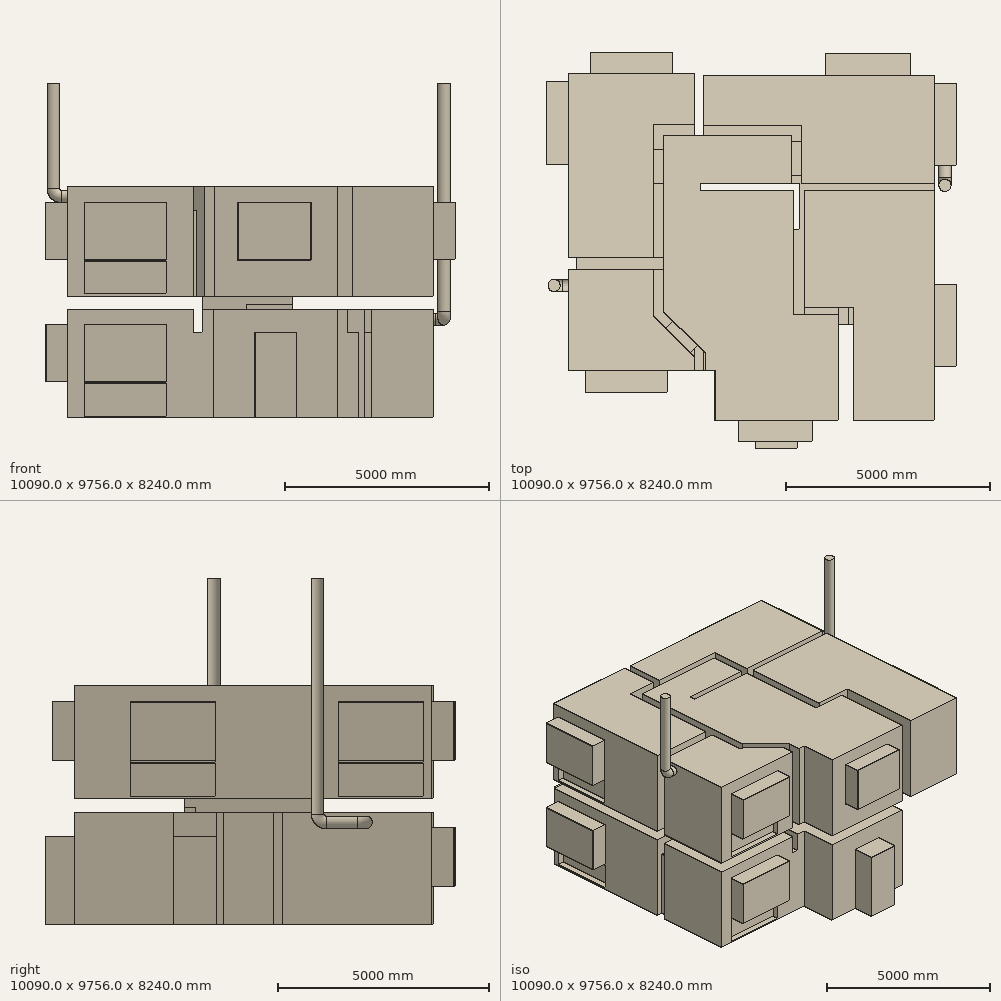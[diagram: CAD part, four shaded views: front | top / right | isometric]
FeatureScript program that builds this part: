
annotation { "Feature Type Name" : "Feature", "Feature Type Description" : "" }
export const myFeature = defineFeature(function(context is Context, id is Id, definition is map)
    precondition{}
    {
        {
            var Q0;
            Q0=qCreatedBy(makeId("Top.planeOp"),FACE);
            var sketch = newSketch(context, id + "F0", { "sketchPlane" : qUnion([Q0])});
            skLineSegment(sketch, "E0.bottom", {"start": v(-1549.14, 3434.73) * mm, "end": v(1546.86, 3434.73) * mm});
            skLineSegment(sketch, "E0.top", {"start": v(-1549.14, -1072.27) * mm, "end": v(1546.86, -1072.27) * mm});
            skLineSegment(sketch, "E0.left", {"start": v(-1549.14, 3434.73) * mm, "end": v(-1549.14, -1072.27) * mm});
            skLineSegment(sketch, "E0.right", {"start": v(1546.86, 3434.73) * mm, "end": v(1546.86, -1072.27) * mm});
            skSolve(sketch);
        }
        {
            var Q0;
            Q0=makeQuery(id+"F0.imprint","IMPRINT",FACE,{"disambiguationData":[TD([[makeQuery(id+"F0.imprint","IMPRINT",EDGE,{"derivedFrom":sQuery(id+"F0.wireOp",EDGE,"E0.bottom")}),-1.0]])]});
            extrude(context, id + "F1", {"entities" : qUnion([Q0]), "depth" : 2680 * mm});
        }
        {
            var Q0;
            Q0=makeQuery(id+"F1.opExtrude","SWEPT_FACE",FACE,{"disambiguationData":[OSD([sQuery(id+"F0.wireOp",EDGE,"E0.bottom")])]});
            var sketch = newSketch(context, id + "F2", { "sketchPlane" : qUnion([Q0])});
            skLineSegment(sketch, "E1.bottom", {"start": v(-1013.86, 2300) * mm, "end": v(1011.14, 2300) * mm});
            skLineSegment(sketch, "E1.top", {"start": v(-1013.86, 900) * mm, "end": v(1011.14, 900) * mm});
            skLineSegment(sketch, "E1.left", {"start": v(-1013.86, 2300) * mm, "end": v(-1013.86, 900) * mm});
            skLineSegment(sketch, "E1.right", {"start": v(1011.14, 2300) * mm, "end": v(1011.14, 900) * mm});
            skSolve(sketch);
        }
        {
            var Q0;
            Q0=qSketchRegion(id+"F2",true);
            extrude(context, id + "F3", {"entities" : qUnion([Q0]), "operationType" : NewBodyOperationType.ADD, "depth" : 532 * mm});
        }
        {
            var Q0;
            Q0=makeQuery(id+"F1.opExtrude","SWEPT_FACE",FACE,{"disambiguationData":[OSD([sQuery(id+"F0.wireOp",EDGE,"E0.left")])]});
            var sketch = newSketch(context, id + "F4", { "sketchPlane" : qUnion([Q0])});
            skLineSegment(sketch, "E2.bottom", {"start": v(-3238.73, 2300) * mm, "end": v(-1213.73, 2300) * mm});
            skLineSegment(sketch, "E2.top", {"start": v(-3238.73, 900) * mm, "end": v(-1213.73, 900) * mm});
            skLineSegment(sketch, "E2.left", {"start": v(-3238.73, 2300) * mm, "end": v(-3238.73, 900) * mm});
            skLineSegment(sketch, "E2.right", {"start": v(-1213.73, 2300) * mm, "end": v(-1213.73, 900) * mm});
            skSolve(sketch);
        }
        {
            var Q0;
            Q0=makeQuery(id+"F4.imprint","IMPRINT",FACE,{"disambiguationData":[TD([[makeQuery(id+"F4.imprint","IMPRINT",EDGE,{"derivedFrom":sQuery(id+"F4.wireOp",EDGE,"E2.bottom")}),-1.0]])]});
            extrude(context, id + "F5", {"entities" : qUnion([Q0]), "operationType" : NewBodyOperationType.ADD, "depth" : 532 * mm});
        }
        {
            var Q0;
            Q0=makeQuery(id+"F1.opExtrude","SWEPT_FACE",FACE,{"disambiguationData":[OSD([sQuery(id+"F0.wireOp",EDGE,"E0.bottom")])]});
            var sketch = newSketch(context, id + "F6", { "sketchPlane" : qUnion([Q0])});
            skLineSegment(sketch, "E3", {"start": v(1011.14, 900) * mm, "end": v(-1013.86, 900) * mm});
            skLineSegment(sketch, "E4.left", {"start": v(-1013.86, 835) * mm, "end": v(-1013.86, 35) * mm});
            skLineSegment(sketch, "E5.bottom", {"start": v(-1013.86, 835) * mm, "end": v(1011.14, 835) * mm});
            skLineSegment(sketch, "E5.top", {"start": v(-1013.86, 35) * mm, "end": v(1011.14, 35) * mm});
            skLineSegment(sketch, "E5.right", {"start": v(1011.14, 835) * mm, "end": v(1011.14, 35) * mm});
            skSolve(sketch);
        }
        {
            var Q0;
            Q0=makeQuery(id+"F6.imprint","IMPRINT",FACE,{"disambiguationData":[TD([[makeQuery(id+"F6.imprint","IMPRINT",EDGE,{"derivedFrom":sQuery(id+"F6.wireOp",EDGE,"E5.bottom")}),-1.0]])]});
            extrude(context, id + "F7", {"entities" : qUnion([Q0]), "operationType" : NewBodyOperationType.REMOVE, "oppositeDirection" : true, "depth" : 200 * mm});
        }
        {
            var Q0;
            Q0=makeQuery(id+"F1.opExtrude","CAP_FACE",FACE,{"disambiguationData":[OSD([sQuery(id+"F0.wireOp",EDGE,"E0.bottom"),sQuery(id+"F0.wireOp",EDGE,"E0.top"),sQuery(id+"F0.wireOp",EDGE,"E0.left"),sQuery(id+"F0.wireOp",EDGE,"E0.right")])],"isStart":true});
            var sketch = newSketch(context, id + "F8", { "sketchPlane" : qUnion([Q0])});
            skLineSegment(sketch, "E6", {"start": v(-1351.14, 1072.27) * mm, "end": v(-1351.14, 1375.27) * mm});
            skLineSegment(sketch, "E7", {"start": v(-1351.14, 1375.27) * mm, "end": v(1348.86, 1375.27) * mm});
            skLineSegment(sketch, "E8", {"start": v(1348.86, 1375.27) * mm, "end": v(1348.86, 1072.27) * mm});
            skLineSegment(sketch, "E9", {"start": v(1348.86, 1072.27) * mm, "end": v(-1351.14, 1072.27) * mm});
            skSolve(sketch);
        }
        {
            var Q0;
            Q0=makeQuery(id+"F8.imprint","IMPRINT",FACE,{"disambiguationData":[TD([[makeQuery(id+"F8.imprint","IMPRINT",EDGE,{"derivedFrom":sQuery(id+"F8.wireOp",EDGE,"E6")}),-1.0]])]});
            extrude(context, id + "F9", {"entities" : qUnion([Q0]), "operationType" : NewBodyOperationType.ADD, "oppositeDirection" : true, "depth" : 2100 * mm});
        }
        {
            var Q0;
            Q0=makeQuery(id+"F9.boolean.opBoolean","MERGE",FACE,{"derivedFrom":[makeQuery(id+"F1.opExtrude","CAP_FACE",FACE,{"disambiguationData":[OSD([sQuery(id+"F0.wireOp",EDGE,"E0.bottom"),sQuery(id+"F0.wireOp",EDGE,"E0.top"),sQuery(id+"F0.wireOp",EDGE,"E0.left"),sQuery(id+"F0.wireOp",EDGE,"E0.right")])],"isStart":true}),makeQuery(id+"F9.opExtrude","CAP_FACE",FACE,{"disambiguationData":[OSD([sQuery(id+"F8.wireOp",EDGE,"E6"),sQuery(id+"F8.wireOp",EDGE,"E7"),sQuery(id+"F8.wireOp",EDGE,"E8"),sQuery(id+"F8.wireOp",EDGE,"E9")])],"isStart":true})]});
            var sketch = newSketch(context, id + "F10", { "sketchPlane" : qUnion([Q0])});
            skLineSegment(sketch, "E10.bottom", {"start": v(-1549.14, 1375.27) * mm, "end": v(1546.86, 1375.27) * mm});
            skLineSegment(sketch, "E10.top", {"start": v(-1549.14, 3872.27) * mm, "end": v(1546.86, 3872.27) * mm});
            skLineSegment(sketch, "E10.left", {"start": v(-1549.14, 1375.27) * mm, "end": v(-1549.14, 3872.27) * mm});
            skLineSegment(sketch, "E10.right", {"start": v(1546.86, 1375.27) * mm, "end": v(1546.86, 3872.27) * mm});
            skLineSegment(sketch, "E11", {"start": v(-1549.14, 1375.27) * mm, "end": v(-1351.14, 1375.27) * mm});
            skSolve(sketch);
        }
        {
            var Q0;
            Q0=qSketchRegion(id+"F10",true);
            extrude(context, id + "F11", {"entities" : qUnion([Q0]), "operationType" : NewBodyOperationType.ADD, "oppositeDirection" : true, "depth" : 2680 * mm});
        }
        {
            var Q0;
            Q0=makeQuery(id+"F11.boolean.opBoolean","MERGE",FACE,{"derivedFrom":[makeQuery(id+"F9.boolean.opBoolean","MERGE",FACE,{"derivedFrom":[makeQuery(id+"F1.opExtrude","CAP_FACE",FACE,{"disambiguationData":[OSD([sQuery(id+"F0.wireOp",EDGE,"E0.bottom"),sQuery(id+"F0.wireOp",EDGE,"E0.top"),sQuery(id+"F0.wireOp",EDGE,"E0.left"),sQuery(id+"F0.wireOp",EDGE,"E0.right")])],"isStart":true}),makeQuery(id+"F9.opExtrude","CAP_FACE",FACE,{"disambiguationData":[OSD([sQuery(id+"F8.wireOp",EDGE,"E6"),sQuery(id+"F8.wireOp",EDGE,"E7"),sQuery(id+"F8.wireOp",EDGE,"E8"),sQuery(id+"F8.wireOp",EDGE,"E9")])],"isStart":true})]}),makeQuery(id+"F11.opExtrude","CAP_FACE",FACE,{"disambiguationData":[OSD([sQuery(id+"F10.wireOp",EDGE,"E10.bottom"),sQuery(id+"F10.wireOp",EDGE,"E10.top"),sQuery(id+"F10.wireOp",EDGE,"E10.left"),sQuery(id+"F10.wireOp",EDGE,"E10.right"),sQuery(id+"F10.wireOp",EDGE,"E11")])],"isStart":true})]});
            var sketch = newSketch(context, id + "F12", { "sketchPlane" : qUnion([Q0])});
            skLineSegment(sketch, "E12.bottom", {"start": v(1546.86, 3872.27) * mm, "end": v(1765.86, 3872.27) * mm});
            skLineSegment(sketch, "E12.top", {"start": v(1546.86, 2526.27) * mm, "end": v(1765.86, 2526.27) * mm});
            skLineSegment(sketch, "E12.left", {"start": v(1546.86, 3872.27) * mm, "end": v(1546.86, 2526.27) * mm});
            skLineSegment(sketch, "E12.right", {"start": v(1765.86, 3872.27) * mm, "end": v(1765.86, 2526.27) * mm});
            skSolve(sketch);
        }
        {
            var Q0;
            Q0=makeQuery(id+"F12.imprint","IMPRINT",FACE,{"disambiguationData":[TD([[makeQuery(id+"F12.imprint","IMPRINT",EDGE,{"derivedFrom":sQuery(id+"F12.wireOp",EDGE,"E12.bottom")}),-1.0]])]});
            extrude(context, id + "F13", {"entities" : qUnion([Q0]), "operationType" : NewBodyOperationType.ADD, "oppositeDirection" : true, "depth" : 2100 * mm});
        }
        {
            var Q0;
            Q0=makeQuery(id+"F13.boolean.opBoolean","MERGE",FACE,{"derivedFrom":[makeQuery(id+"F11.opExtrude","SWEPT_FACE",FACE,{"disambiguationData":[OSD([sQuery(id+"F10.wireOp",EDGE,"E10.top")])]}),makeQuery(id+"F13.opExtrude","SWEPT_FACE",FACE,{"disambiguationData":[OSD([sQuery(id+"F12.wireOp",EDGE,"E12.bottom")])]})]});
            var sketch = newSketch(context, id + "F14", { "sketchPlane" : qUnion([Q0])});
            skLineSegment(sketch, "E13.bottom", {"start": v(-1134.15, 2296.53) * mm, "end": v(890.85, 2296.53) * mm});
            skLineSegment(sketch, "E13.top", {"start": v(-1134.15, 896.53) * mm, "end": v(890.85, 896.53) * mm});
            skLineSegment(sketch, "E13.left", {"start": v(-1134.15, 2296.53) * mm, "end": v(-1134.15, 896.53) * mm});
            skLineSegment(sketch, "E13.right", {"start": v(890.85, 2296.53) * mm, "end": v(890.85, 896.53) * mm});
            skSolve(sketch);
        }
        {
            var Q0;
            Q0=makeQuery(id+"F14.imprint","IMPRINT",FACE,{"disambiguationData":[TD([[makeQuery(id+"F14.imprint","IMPRINT",EDGE,{"derivedFrom":sQuery(id+"F14.wireOp",EDGE,"E13.bottom")}),-1.0]])]});
            extrude(context, id + "F15", {"entities" : qUnion([Q0]), "operationType" : NewBodyOperationType.ADD, "depth" : 532 * mm});
        }
        {
            var Q0;
            Q0=makeQuery(id+"F12.imprint","IMPRINT",FACE,{"disambiguationData":[TD([[makeQuery(id+"F12.imprint","IMPRINT",EDGE,{"derivedFrom":sQuery(id+"F12.wireOp",EDGE,"E12.bottom")}),-1.0]])]});
            var sketch = newSketch(context, id + "F16", { "sketchPlane" : qUnion([Q0])});
            skLineSegment(sketch, "E14", {"start": v(1765.86, 3872.27) * mm, "end": v(2057.86, 3872.27) * mm});
            skLineSegment(sketch, "E15", {"start": v(2057.86, 3872.27) * mm, "end": v(2057.86, 5091.27) * mm});
            skLineSegment(sketch, "E16", {"start": v(1765.86, 3872.27) * mm, "end": v(1765.86, 2474.27) * mm});
            skLineSegment(sketch, "E17", {"start": v(1765.86, 2474.27) * mm, "end": v(2915.86, 2474.27) * mm});
            skLineSegment(sketch, "E18", {"start": v(2915.86, 2474.27) * mm, "end": v(2915.86, 2739.27) * mm});
            skLineSegment(sketch, "E19", {"start": v(2915.86, 2739.27) * mm, "end": v(5096.86, 2739.27) * mm});
            skLineSegment(sketch, "E20", {"start": v(5096.86, 2739.27) * mm, "end": v(5096.86, 5091.27) * mm});
            skLineSegment(sketch, "E21", {"start": v(2057.86, 5091.27) * mm, "end": v(5096.86, 5091.27) * mm});
            skSolve(sketch);
        }
        {
            var Q0;
            {var subQ1=sQuery(id+"F16.wireOp",EDGE,"E14");Q0=makeQuery(id+"F16.imprint","IMPRINT",FACE,{"disambiguationData":[TD([[makeQuery(id+"F16.imprint","IMPRINT",EDGE,{"derivedFrom":subQ1}),-1.0]])]});}
            extrude(context, id + "F17", {"entities" : qUnion([Q0]), "operationType" : NewBodyOperationType.ADD, "oppositeDirection" : true, "depth" : 2680 * mm});
        }
        {
            var Q0;
            Q0=makeQuery(id+"F17.boolean.opBoolean","MERGE",FACE,{"derivedFrom":[makeQuery(id+"F13.boolean.opBoolean","MERGE",FACE,{"derivedFrom":[makeQuery(id+"F11.boolean.opBoolean","MERGE",FACE,{"derivedFrom":[makeQuery(id+"F9.boolean.opBoolean","MERGE",FACE,{"derivedFrom":[makeQuery(id+"F1.opExtrude","CAP_FACE",FACE,{"disambiguationData":[OSD([sQuery(id+"F0.wireOp",EDGE,"E0.bottom"),sQuery(id+"F0.wireOp",EDGE,"E0.top"),sQuery(id+"F0.wireOp",EDGE,"E0.left"),sQuery(id+"F0.wireOp",EDGE,"E0.right")])],"isStart":true}),makeQuery(id+"F9.opExtrude","CAP_FACE",FACE,{"disambiguationData":[OSD([sQuery(id+"F8.wireOp",EDGE,"E6"),sQuery(id+"F8.wireOp",EDGE,"E7"),sQuery(id+"F8.wireOp",EDGE,"E8"),sQuery(id+"F8.wireOp",EDGE,"E9")])],"isStart":true})]}),makeQuery(id+"F11.opExtrude","CAP_FACE",FACE,{"disambiguationData":[OSD([sQuery(id+"F10.wireOp",EDGE,"E10.bottom"),sQuery(id+"F10.wireOp",EDGE,"E10.top"),sQuery(id+"F10.wireOp",EDGE,"E10.left"),sQuery(id+"F10.wireOp",EDGE,"E10.right"),sQuery(id+"F10.wireOp",EDGE,"E11")])],"isStart":true})]}),makeQuery(id+"F13.opExtrude","CAP_FACE",FACE,{"disambiguationData":[OSD([sQuery(id+"F12.wireOp",EDGE,"E12.bottom"),sQuery(id+"F12.wireOp",EDGE,"E12.top"),sQuery(id+"F12.wireOp",EDGE,"E12.left"),sQuery(id+"F12.wireOp",EDGE,"E12.right")])],"isStart":true})]}),makeQuery(id+"F17.opExtrude","CAP_FACE",FACE,{"disambiguationData":[OSD([sQuery(id+"F16.wireOp",EDGE,"E14"),sQuery(id+"F16.wireOp",EDGE,"E15"),sQuery(id+"F16.wireOp",EDGE,"E16"),sQuery(id+"F16.wireOp",EDGE,"E17"),sQuery(id+"F16.wireOp",EDGE,"E18"),sQuery(id+"F16.wireOp",EDGE,"E19"),sQuery(id+"F16.wireOp",EDGE,"E20"),sQuery(id+"F16.wireOp",EDGE,"E21")])],"isStart":true})]});
            var sketch = newSketch(context, id + "F18", { "sketchPlane" : qUnion([Q0])});
            skLineSegment(sketch, "E22.bottom", {"start": v(3064.86, 5091.27) * mm, "end": v(4089.86, 5091.27) * mm});
            skLineSegment(sketch, "E22.top", {"start": v(3064.86, 5789.27) * mm, "end": v(4089.86, 5789.27) * mm});
            skLineSegment(sketch, "E22.left", {"start": v(3064.86, 5091.27) * mm, "end": v(3064.86, 5789.27) * mm});
            skLineSegment(sketch, "E22.right", {"start": v(4089.86, 5091.27) * mm, "end": v(4089.86, 5789.27) * mm});
            skSolve(sketch);
        }
        {
            var Q0;
            Q0=makeQuery(id+"F18.imprint","IMPRINT",FACE,{"disambiguationData":[TD([[makeQuery(id+"F18.imprint","IMPRINT",EDGE,{"derivedFrom":sQuery(id+"F18.wireOp",EDGE,"E22.bottom")}),1.0]])]});
            extrude(context, id + "F19", {"entities" : qUnion([Q0]), "operationType" : NewBodyOperationType.ADD, "oppositeDirection" : true, "depth" : 2100 * mm});
        }
        {
            var Q0;
            {var subQ0=sQuery(id+"F16.wireOp",EDGE,"E14");Q0=makeQuery(id+"F16.imprint","IMPRINT",FACE,{"disambiguationData":[TD([[makeQuery(id+"F16.imprint","IMPRINT",EDGE,{"derivedFrom":subQ0}),-1.0]])]});}
            var sketch = newSketch(context, id + "F20", { "sketchPlane" : qUnion([Q0])});
            skLineSegment(sketch, "E23.bottom", {"start": v(1765.86, 2474.27) * mm, "end": v(3985.86, 2474.27) * mm});
            skLineSegment(sketch, "E23.top", {"start": v(1765.86, -565.73) * mm, "end": v(3985.86, -565.73) * mm});
            skLineSegment(sketch, "E23.left", {"start": v(1765.86, 2474.27) * mm, "end": v(1765.86, -565.73) * mm});
            skLineSegment(sketch, "E23.right", {"start": v(3985.86, 2474.27) * mm, "end": v(3985.86, -565.73) * mm});
            skSolve(sketch);
        }
        {
            var Q0;
            Q0=makeQuery(id+"F20.imprint","IMPRINT",FACE,{"disambiguationData":[TD([[makeQuery(id+"F20.imprint","IMPRINT",EDGE,{"derivedFrom":sQuery(id+"F20.wireOp",EDGE,"E23.top")}),1.0]])]});
            extrude(context, id + "F21", {"entities" : qUnion([Q0]), "oppositeDirection" : true, "depth" : 3000 * mm});
        }
        {
            var Q0;
            Q0=makeQuery(id+"F21.opExtrude","SWEPT_FACE",FACE,{"disambiguationData":[OSD([sQuery(id+"F20.wireOp",EDGE,"E23.left")])]});
            var sketch = newSketch(context, id + "F22", { "sketchPlane" : qUnion([Q0])});
            skLineSegment(sketch, "E24.MirrorCS", {"start": v(1199.27, 1020) * mm, "end": v(944.27, 1020) * mm});
            skLineSegment(sketch, "E25.MirrorCS", {"start": v(1709.27, 680) * mm, "end": v(1454.27, 680) * mm});
            skLineSegment(sketch, "E26.MirrorCS", {"start": v(2219.27, 340) * mm, "end": v(1964.27, 340) * mm});
            skLineSegment(sketch, "E27.MirrorCS", {"start": v(2474.27, 0) * mm, "end": v(2219.27, 0) * mm});
            skLineSegment(sketch, "E28.MirrorCS", {"start": v(1964.27, 340) * mm, "end": v(1964.27, 510) * mm});
            skLineSegment(sketch, "E29.MirrorCS", {"start": v(1454.27, 680) * mm, "end": v(1454.27, 850) * mm});
            skLineSegment(sketch, "E30.MirrorCS", {"start": v(1709.27, 510) * mm, "end": v(1709.27, 680) * mm});
            skLineSegment(sketch, "E31.MirrorCS", {"start": v(1199.27, 850) * mm, "end": v(1199.27, 1020) * mm});
            skLineSegment(sketch, "E32.MirrorCS", {"start": v(1454.27, 850) * mm, "end": v(1199.27, 850) * mm});
            skLineSegment(sketch, "E33.MirrorCS", {"start": v(-565.73, 1530) * mm, "end": v(-565.73, 1330) * mm});
            skLineSegment(sketch, "E34.MirrorCS", {"start": v(2219.27, 170) * mm, "end": v(2219.27, 340) * mm});
            skLineSegment(sketch, "E35.MirrorCS", {"start": v(2474.27, 170) * mm, "end": v(2219.27, 170) * mm});
            skLineSegment(sketch, "E36.MirrorCS", {"start": v(1964.27, 510) * mm, "end": v(1709.27, 510) * mm});
            skLineSegment(sketch, "E37.MirrorCS", {"start": v(2474.27, 0) * mm, "end": v(2474.27, 170) * mm});
            skLineSegment(sketch, "E38.MirrorCS", {"start": v(2474.27, 170) * mm, "end": v(2474.27, 0) * mm});
            skLineSegment(sketch, "E39", {"start": v(2219.27, 0) * mm, "end": v(179.27, 1330) * mm});
            skLineSegment(sketch, "E40", {"start": v(944.27, 1020) * mm, "end": v(944.27, 1190) * mm});
            skLineSegment(sketch, "E41", {"start": v(944.27, 1190) * mm, "end": v(689.27, 1190) * mm});
            skLineSegment(sketch, "E42", {"start": v(689.27, 1190) * mm, "end": v(689.27, 1330) * mm});
            skLineSegment(sketch, "E43", {"start": v(689.27, 1330) * mm, "end": v(434.27, 1330) * mm});
            skLineSegment(sketch, "E44", {"start": v(434.27, 1330) * mm, "end": v(434.27, 1530) * mm});
            skLineSegment(sketch, "E45", {"start": v(434.27, 1530) * mm, "end": v(-565.73, 1530) * mm});
            skLineSegment(sketch, "E46", {"start": v(-565.73, 1330) * mm, "end": v(179.27, 1330) * mm});
            skSolve(sketch);
        }
        {
            var Q0;
            Q0=qSketchRegion(id+"F22",true);
            extrude(context, id + "F23", {"entities" : qUnion([Q0]), "operationType" : NewBodyOperationType.REMOVE, "oppositeDirection" : true, "depth" : 1110 * mm});
        }
        {
            var Q0;
            Q0=makeQuery(id+"F21.opExtrude","SWEPT_FACE",FACE,{"disambiguationData":[OSD([sQuery(id+"F20.wireOp",EDGE,"E23.right")])]});
            var sketch = newSketch(context, id + "F24", { "sketchPlane" : qUnion([Q0])});
            skLineSegment(sketch, "E47", {"start": v(565.73, 1530) * mm, "end": v(-689.27, 1530) * mm});
            skLineSegment(sketch, "E48", {"start": v(-689.27, 1530) * mm, "end": v(-689.27, 1710) * mm});
            skLineSegment(sketch, "E49", {"start": v(-689.27, 1710) * mm, "end": v(-944.27, 1710) * mm});
            skLineSegment(sketch, "E50", {"start": v(-944.27, 1710) * mm, "end": v(-944.27, 1890) * mm});
            skLineSegment(sketch, "E51", {"start": v(-944.27, 1890) * mm, "end": v(-1199.27, 1890) * mm});
            skLineSegment(sketch, "E52", {"start": v(-1199.27, 1890) * mm, "end": v(-1199.27, 2070) * mm});
            skLineSegment(sketch, "E53", {"start": v(-1199.27, 2070) * mm, "end": v(-1454.27, 2070) * mm});
            skLineSegment(sketch, "E54", {"start": v(-1454.27, 2070) * mm, "end": v(-1454.27, 2250) * mm});
            skLineSegment(sketch, "E55", {"start": v(-1454.27, 2250) * mm, "end": v(-1709.27, 2250) * mm});
            skLineSegment(sketch, "E56", {"start": v(-1709.27, 2430) * mm, "end": v(-1709.27, 2250) * mm});
            skLineSegment(sketch, "E57", {"start": v(565.73, 1530) * mm, "end": v(565.73, 1330) * mm});
            skLineSegment(sketch, "E58", {"start": v(-689.27, 1330) * mm, "end": v(565.73, 1330) * mm});
            skLineSegment(sketch, "E59", {"start": v(-1709.27, 2430) * mm, "end": v(-1964.27, 2430) * mm});
            skLineSegment(sketch, "E60", {"start": v(-1964.27, 2430) * mm, "end": v(-1964.27, 2610) * mm});
            skLineSegment(sketch, "E61", {"start": v(-1964.27, 2610) * mm, "end": v(-2219.27, 2610) * mm});
            skLineSegment(sketch, "E62", {"start": v(-2219.27, 2610) * mm, "end": v(-2219.27, 2790) * mm});
            skLineSegment(sketch, "E63", {"start": v(-2219.27, 2790) * mm, "end": v(-2474.27, 2790) * mm});
            skLineSegment(sketch, "E64", {"start": v(-2474.27, 2651.89) * mm, "end": v(-689.27, 1330) * mm});
            skLineSegment(sketch, "E65", {"start": v(-2474.27, 2651.89) * mm, "end": v(-2474.27, 2790) * mm});
            skLineSegment(sketch, "E66", {"start": v(565.73, 1330) * mm, "end": v(565.73, 1530) * mm});
            skLineSegment(sketch, "E67", {"start": v(-689.27, 1530) * mm, "end": v(565.73, 1530) * mm});
            skSolve(sketch);
        }
        {
            var Q0;
            Q0=makeQuery(id+"F24.imprint","IMPRINT",FACE,{"disambiguationData":[TD([[makeQuery(id+"F24.imprint","IMPRINT",EDGE,{"derivedFrom":sQuery(id+"F24.wireOp",EDGE,"E48")}),1.0]])]});
            extrude(context, id + "F25", {"entities" : qUnion([Q0]), "operationType" : NewBodyOperationType.REMOVE, "oppositeDirection" : true, "depth" : 1120 * mm});
        }
        {
            var Q0;
            Q0=makeQuery(id+"F17.opExtrude","CAP_FACE",FACE,{"disambiguationData":[OSD([sQuery(id+"F16.wireOp",EDGE,"E14"),sQuery(id+"F16.wireOp",EDGE,"E15"),sQuery(id+"F16.wireOp",EDGE,"E16"),sQuery(id+"F16.wireOp",EDGE,"E17"),sQuery(id+"F16.wireOp",EDGE,"E18"),sQuery(id+"F16.wireOp",EDGE,"E19"),sQuery(id+"F16.wireOp",EDGE,"E20"),sQuery(id+"F16.wireOp",EDGE,"E21")])],"isStart":false});
            var sketch = newSketch(context, id + "F26", { "sketchPlane" : qUnion([Q0])});
            skLineSegment(sketch, "E68", {"start": v(5096.86, -2739.27) * mm, "end": v(5356.86, -2739.27) * mm});
            skLineSegment(sketch, "E69", {"start": v(5221.86, -1714.27) * mm, "end": v(5221.86, -1554.27) * mm});
            skLineSegment(sketch, "E70", {"start": v(5221.86, -1554.27) * mm, "end": v(5771.86, -1554.27) * mm});
            skLineSegment(sketch, "E71", {"start": v(5771.86, -1554.27) * mm, "end": v(5771.86, -1454.27) * mm});
            skLineSegment(sketch, "E72", {"start": v(5771.86, -629.27) * mm, "end": v(5771.86, -354.27) * mm});
            skLineSegment(sketch, "E73", {"start": v(5771.86, -354.27) * mm, "end": v(5421.86, -354.27) * mm});
            skLineSegment(sketch, "E74", {"start": v(5421.86, -354.27) * mm, "end": v(5421.86, -142.27) * mm});
            skLineSegment(sketch, "E75", {"start": v(7471.86, 3404.73) * mm, "end": v(6893.86, 3404.73) * mm});
            skLineSegment(sketch, "E76", {"start": v(4681.86, 3404.73) * mm, "end": v(1765.86, 3404.73) * mm});
            skLineSegment(sketch, "E77", {"start": v(1765.86, 3404.73) * mm, "end": v(1765.86, 747.73) * mm});
            skLineSegment(sketch, "E78", {"start": v(1765.86, 747.73) * mm, "end": v(4146.86, 747.73) * mm});
            skLineSegment(sketch, "E79", {"start": v(4146.86, 747.73) * mm, "end": v(4146.86, -384.27) * mm});
            skLineSegment(sketch, "E80", {"start": v(5096.86, -2739.27) * mm, "end": v(2915.86, -2739.27) * mm});
            skLineSegment(sketch, "E81", {"start": v(2915.86, -2739.27) * mm, "end": v(2915.86, -2474.27) * mm});
            skLineSegment(sketch, "E82", {"start": v(2915.86, -2474.27) * mm, "end": v(3985.86, -2474.27) * mm});
            skLineSegment(sketch, "E83", {"start": v(3985.86, -2474.27) * mm, "end": v(3985.86, -384.27) * mm});
            skLineSegment(sketch, "E84", {"start": v(3985.86, -384.27) * mm, "end": v(4146.86, -384.27) * mm});
            skLineSegment(sketch, "E85", {"start": v(5771.86, -629.27) * mm, "end": v(5771.86, -1454.27) * mm});
            skLineSegment(sketch, "E86", {"start": v(4681.86, 3404.73) * mm, "end": v(6893.86, 3404.73) * mm});
            skLineSegment(sketch, "E87", {"start": v(5356.86, -2739.27) * mm, "end": v(5356.86, -1714.27) * mm});
            skLineSegment(sketch, "E88", {"start": v(5356.86, -1714.27) * mm, "end": v(5221.86, -1714.27) * mm});
            skLineSegment(sketch, "E89", {"start": v(7471.86, 3404.73) * mm, "end": v(7471.86, -142.27) * mm});
            skLineSegment(sketch, "E90", {"start": v(5421.86, -142.27) * mm, "end": v(7471.86, -142.27) * mm});
            skSolve(sketch);
        }
        {
            var Q0;
            Q0=makeQuery(id+"F26.imprint","IMPRINT",FACE,{"disambiguationData":[TD([[makeQuery(id+"F26.imprint","IMPRINT",EDGE,{"derivedFrom":sQuery(id+"F26.wireOp",EDGE,"E68")}),1.0]])]});
            extrude(context, id + "F27", {"entities" : qUnion([Q0]), "oppositeDirection" : true, "depth" : 2680 * mm});
        }
        {
            var Q0;
            Q0=makeQuery(id+"F27.opExtrude","SWEPT_FACE",FACE,{"disambiguationData":[OSD([sQuery(id+"F26.wireOp",EDGE,"E75"),sQuery(id+"F26.wireOp",EDGE,"E76"),sQuery(id+"F26.wireOp",EDGE,"E86")])]});
            var sketch = newSketch(context, id + "F28", { "sketchPlane" : qUnion([Q0])});
            skLineSegment(sketch, "E91.bottom", {"start": v(-6883.86, 2300) * mm, "end": v(-4883.86, 2300) * mm});
            skLineSegment(sketch, "E91.top", {"start": v(-6883.86, 900) * mm, "end": v(-4883.86, 900) * mm});
            skLineSegment(sketch, "E91.left", {"start": v(-6883.86, 2300) * mm, "end": v(-6883.86, 900) * mm});
            skLineSegment(sketch, "E91.right", {"start": v(-4883.86, 2300) * mm, "end": v(-4883.86, 900) * mm});
            skSolve(sketch);
        }
        {
            var Q0;
            Q0=makeQuery(id+"F28.imprint","IMPRINT",FACE,{"disambiguationData":[TD([[makeQuery(id+"F28.imprint","IMPRINT",EDGE,{"derivedFrom":sQuery(id+"F28.wireOp",EDGE,"E91.bottom")}),-1.0]])]});
            extrude(context, id + "F29", {"entities" : qUnion([Q0]), "operationType" : NewBodyOperationType.ADD, "depth" : 532 * mm});
        }
        {
            var Q0;
            Q0=makeQuery(id+"F27.opExtrude","SWEPT_FACE",FACE,{"disambiguationData":[OSD([sQuery(id+"F26.wireOp",EDGE,"E71"),sQuery(id+"F26.wireOp",EDGE,"E72"),sQuery(id+"F26.wireOp",EDGE,"E85")])]});
            var sketch = newSketch(context, id + "F30", { "sketchPlane" : qUnion([Q0])});
            skLineSegment(sketch, "E92.bottom", {"start": v(-1454.27, 2100) * mm, "end": v(-629.27, 2100) * mm});
            skLineSegment(sketch, "E92.top", {"start": v(-1454.27, 0) * mm, "end": v(-629.27, 0) * mm});
            skLineSegment(sketch, "E92.left", {"start": v(-1454.27, 2100) * mm, "end": v(-1454.27, 0) * mm});
            skLineSegment(sketch, "E92.right", {"start": v(-629.27, 2100) * mm, "end": v(-629.27, 0) * mm});
            skSolve(sketch);
        }
        {
            var Q0;
            Q0=makeQuery(id+"F30.imprint","IMPRINT",FACE,{"disambiguationData":[TD([[makeQuery(id+"F30.imprint","IMPRINT",EDGE,{"derivedFrom":sQuery(id+"F30.wireOp",EDGE,"E92.bottom")}),-1.0]])]});
            extrude(context, id + "F31", {"entities" : qUnion([Q0]), "operationType" : NewBodyOperationType.ADD, "depth" : 160 * mm});
        }
        {
            var Q0;
            Q0=makeQuery(id+"F31.opExtrude","CAP_FACE",FACE,{"disambiguationData":[OSD([sQuery(id+"F30.wireOp",EDGE,"E92.bottom"),sQuery(id+"F30.wireOp",EDGE,"E92.top"),sQuery(id+"F30.wireOp",EDGE,"E92.left"),sQuery(id+"F30.wireOp",EDGE,"E92.right")])],"isStart":false});
            var sketch = newSketch(context, id + "F32", { "sketchPlane" : qUnion([Q0])});
            skLineSegment(sketch, "E93.bottom", {"start": v(-1554.27, 2680) * mm, "end": v(-354.27, 2680) * mm});
            skLineSegment(sketch, "E93.top", {"start": v(-1554.27, 0) * mm, "end": v(-354.27, 0) * mm});
            skLineSegment(sketch, "E93.left", {"start": v(-1554.27, 2680) * mm, "end": v(-1554.27, 0) * mm});
            skLineSegment(sketch, "E93.right", {"start": v(-354.27, 2680) * mm, "end": v(-354.27, 0) * mm});
            skSolve(sketch);
        }
        {
            var Q0;
            Q0=qSketchRegion(id+"F32",true);
            extrude(context, id + "F33", {"entities" : qUnion([Q0]), "operationType" : NewBodyOperationType.ADD, "depth" : 1540 * mm});
        }
        {
            var Q0;
            Q0=makeQuery(id+"F1.opExtrude","SWEPT_BODY",BODY,{"disambiguationData":[OSD([sQuery(id+"F0.wireOp",EDGE,"E0.bottom"),sQuery(id+"F0.wireOp",EDGE,"E0.top"),sQuery(id+"F0.wireOp",EDGE,"E0.left"),sQuery(id+"F0.wireOp",EDGE,"E0.right")])]});
            var Q1;
            Q1=makeQuery(id+"F27.opExtrude","SWEPT_BODY",BODY,{"disambiguationData":[OSD([sQuery(id+"F26.wireOp",EDGE,"E68"),sQuery(id+"F26.wireOp",EDGE,"f08b4c50-08dc-44d1-91bd-df31dd3f817a"),sQuery(id+"F26.wireOp",EDGE,"f896f5a7-1bc8-498b-a9e9-afe6711b9f40"),sQuery(id+"F26.wireOp",EDGE,"E69"),sQuery(id+"F26.wireOp",EDGE,"E70"),sQuery(id+"F26.wireOp",EDGE,"E71"),sQuery(id+"F26.wireOp",EDGE,"E72"),sQuery(id+"F26.wireOp",EDGE,"E73"),sQuery(id+"F26.wireOp",EDGE,"E74"),sQuery(id+"F26.wireOp",EDGE,"4dea9934-df3e-44db-ac8b-cfe9eaf94726"),sQuery(id+"F26.wireOp",EDGE,"69e68077-ab11-4f7d-8ed4-810636c2d2b1"),sQuery(id+"F26.wireOp",EDGE,"E75"),sQuery(id+"F26.wireOp",EDGE,"E76"),sQuery(id+"F26.wireOp",EDGE,"E77"),sQuery(id+"F26.wireOp",EDGE,"E78"),sQuery(id+"F26.wireOp",EDGE,"E79"),sQuery(id+"F26.wireOp",EDGE,"E80"),sQuery(id+"F26.wireOp",EDGE,"E81"),sQuery(id+"F26.wireOp",EDGE,"E82"),sQuery(id+"F26.wireOp",EDGE,"E83"),sQuery(id+"F26.wireOp",EDGE,"E84"),sQuery(id+"F26.wireOp",EDGE,"de4f6d5e-2732-43ff-8072-bc847a33fe50"),sQuery(id+"F26.wireOp",EDGE,"2b71e373-8316-4eaa-b8c1-09a88fac9cdd"),sQuery(id+"F26.wireOp",EDGE,"9742d433-c769-4375-8eee-a89ad4486bd9"),sQuery(id+"F26.wireOp",EDGE,"E85"),sQuery(id+"F26.wireOp",EDGE,"E86")])]});
            booleanBodies(context, id + "F34", {"operationType" : BooleanOperationType.UNION, "tools" : qUnion([Q0, Q1])});
        }
        {
            var Q0;
            Q0=makeQuery(id+"F21.opExtrude","CAP_FACE",FACE,{"disambiguationData":[OSD([sQuery(id+"F20.wireOp",EDGE,"E23.bottom"),sQuery(id+"F20.wireOp",EDGE,"E23.top"),sQuery(id+"F20.wireOp",EDGE,"E23.left"),sQuery(id+"F20.wireOp",EDGE,"E23.right")])],"isStart":false});
            var sketch = newSketch(context, id + "F35", { "sketchPlane" : qUnion([Q0])});
            skSolve(sketch);
        }
        {
            var Q0;
            Q0=makeQuery(id+"F27.opExtrude","SWEPT_FACE",FACE,{"disambiguationData":[OSD([sQuery(id+"F26.wireOp",EDGE,"E87")])]});
            var sketch = newSketch(context, id + "F36", { "sketchPlane" : qUnion([Q0])});
            skLineSegment(sketch, "E94.bottom", {"start": v(-2739.27, 0) * mm, "end": v(-1714.27, 0) * mm});
            skLineSegment(sketch, "E94.top", {"start": v(-2739.27, 2100) * mm, "end": v(-1714.27, 2100) * mm});
            skLineSegment(sketch, "E94.left", {"start": v(-2739.27, 0) * mm, "end": v(-2739.27, 2100) * mm});
            skLineSegment(sketch, "E94.right", {"start": v(-1714.27, 0) * mm, "end": v(-1714.27, 2100) * mm});
            skSolve(sketch);
        }
        {
            var Q0;
            Q0=makeQuery(id+"F36.imprint","IMPRINT",FACE,{"disambiguationData":[TD([[makeQuery(id+"F36.imprint","IMPRINT",EDGE,{"derivedFrom":sQuery(id+"F36.wireOp",EDGE,"E94.bottom")}),1.0]])]});
            extrude(context, id + "F37", {"entities" : qUnion([Q0]), "operationType" : NewBodyOperationType.ADD, "depth" : 260 * mm});
        }
        {
            var Q0;
            Q0=makeQuery(id+"F35.imprint","IMPRINT",FACE,{"disambiguationData":[TD([[makeQuery(id+"F35.imprint","IMPRINT",EDGE,{"derivedFrom":makeQuery(id+"F21.opExtrude","CAP_EDGE",EDGE,{"disambiguationData":[OSD([sQuery(id+"F20.wireOp",EDGE,"E23.bottom")])],"isStart":false})}),1.0]])]});
            var sketch = newSketch(context, id + "F38", { "sketchPlane" : qUnion([Q0])});
            skLineSegment(sketch, "E95", {"start": v(3985.86, -2474.27) * mm, "end": v(5105.86, -2474.27) * mm});
            skLineSegment(sketch, "E96", {"start": v(5105.86, -2474.27) * mm, "end": v(5105.86, -5091.27) * mm});
            skLineSegment(sketch, "E97", {"start": v(5105.86, -5091.27) * mm, "end": v(2065.86, -5091.27) * mm});
            skLineSegment(sketch, "E98", {"start": v(2065.86, -5091.27) * mm, "end": v(2065.86, -3872.27) * mm});
            skLineSegment(sketch, "E99", {"start": v(2065.86, -3872.27) * mm, "end": v(1824.86, -3872.27) * mm});
            skLineSegment(sketch, "E100", {"start": v(1824.86, -3872.27) * mm, "end": v(1824.86, -3437.27) * mm});
            skLineSegment(sketch, "E101", {"start": v(1713.86, 747.73) * mm, "end": v(3936.86, 747.73) * mm});
            skLineSegment(sketch, "E102", {"start": v(3936.86, 747.73) * mm, "end": v(3936.86, 1924.73) * mm});
            skLineSegment(sketch, "E103", {"start": v(3936.86, 1924.73) * mm, "end": v(800.86, 1924.73) * mm});
            skLineSegment(sketch, "E104", {"start": v(800.86, 1924.73) * mm, "end": v(800.86, -2424.27) * mm});
            skLineSegment(sketch, "E105", {"start": v(800.86, -2424.27) * mm, "end": v(1824.86, -3437.27) * mm});
            skLineSegment(sketch, "E106", {"start": v(1713.86, 747.73) * mm, "end": v(1713.86, 565.73) * mm});
            skLineSegment(sketch, "E107", {"start": v(1713.86, 565.73) * mm, "end": v(3985.86, 565.73) * mm});
            skLineSegment(sketch, "E108", {"start": v(3985.86, -2474.27) * mm, "end": v(3985.86, 565.73) * mm});
            skSolve(sketch);
        }
        {
            var Q0;
            Q0=makeQuery(id+"F38.imprint","IMPRINT",FACE,{"disambiguationData":[TD([[makeQuery(id+"F38.imprint","IMPRINT",EDGE,{"derivedFrom":sQuery(id+"F38.wireOp",EDGE,"E95")}),-1.0]])]});
            var Q1;
            Q1=makeQuery(id+"F35.imprint","IMPRINT",FACE,{"disambiguationData":[TD([[makeQuery(id+"F35.imprint","IMPRINT",EDGE,{"derivedFrom":makeQuery(id+"F21.opExtrude","CAP_EDGE",EDGE,{"disambiguationData":[OSD([sQuery(id+"F20.wireOp",EDGE,"E23.bottom")])],"isStart":false})}),1.0]])]});
            extrude(context, id + "F39", {"entities" : qUnion([Q0, Q1]), "depth" : 2700 * mm});
        }
        {
            var Q0;
            Q0=makeQuery(id+"F39.opExtrude","SWEPT_BODY",BODY,{"disambiguationData":[OSD([sQuery(id+"F20.wireOp",EDGE,"E23.bottom"),sQuery(id+"F20.wireOp",EDGE,"E23.left"),sQuery(id+"F38.wireOp",EDGE,"E95"),sQuery(id+"F38.wireOp",EDGE,"E96"),sQuery(id+"F38.wireOp",EDGE,"E97"),sQuery(id+"F38.wireOp",EDGE,"E98"),sQuery(id+"F38.wireOp",EDGE,"E99"),sQuery(id+"F38.wireOp",EDGE,"E100"),sQuery(id+"F38.wireOp",EDGE,"E101"),sQuery(id+"F38.wireOp",EDGE,"E102"),sQuery(id+"F38.wireOp",EDGE,"E103"),sQuery(id+"F38.wireOp",EDGE,"E104"),sQuery(id+"F38.wireOp",EDGE,"E105"),sQuery(id+"F38.wireOp",EDGE,"E106"),sQuery(id+"F38.wireOp",EDGE,"E107")])]});
            var Q1;
            Q1=makeQuery(id+"F39.opExtrude","SWEPT_BODY",BODY,{"disambiguationData":[OSD([sQuery(id+"F20.wireOp",EDGE,"E23.bottom"),sQuery(id+"F20.wireOp",EDGE,"E23.top"),sQuery(id+"F20.wireOp",EDGE,"E23.left"),sQuery(id+"F20.wireOp",EDGE,"E23.right")])]});
            booleanBodies(context, id + "F40", {"operationType" : BooleanOperationType.UNION, "tools" : qUnion([Q0, Q1])});
        }
        {
            var Q0;
            Q0=makeQuery(id+"F39.opExtrude","SWEPT_FACE",FACE,{"disambiguationData":[OSD([sQuery(id+"F38.wireOp",EDGE,"E104")])]});
            var sketch = newSketch(context, id + "F41", { "sketchPlane" : qUnion([Q0])});
            skLineSegment(sketch, "E109.bottom", {"start": v(-1576.73, 5100) * mm, "end": v(-726.73, 5100) * mm});
            skLineSegment(sketch, "E109.top", {"start": v(-1576.73, 3000) * mm, "end": v(-726.73, 3000) * mm});
            skLineSegment(sketch, "E109.left", {"start": v(-1576.73, 5100) * mm, "end": v(-1576.73, 3000) * mm});
            skLineSegment(sketch, "E109.right", {"start": v(-726.73, 5100) * mm, "end": v(-726.73, 3000) * mm});
            skSolve(sketch);
        }
        {
            var Q0;
            Q0=makeQuery(id+"F41.imprint","IMPRINT",FACE,{"disambiguationData":[TD([[makeQuery(id+"F41.imprint","IMPRINT",EDGE,{"derivedFrom":sQuery(id+"F41.wireOp",EDGE,"E109.bottom")}),-1.0]])]});
            extrude(context, id + "F42", {"entities" : qUnion([Q0]), "operationType" : NewBodyOperationType.ADD, "depth" : 255 * mm});
        }
        {
            var Q0;
            Q0=makeQuery(id+"F38.imprint","IMPRINT",FACE,{"disambiguationData":[TD([[makeQuery(id+"F38.imprint","IMPRINT",EDGE,{"derivedFrom":sQuery(id+"F38.wireOp",EDGE,"E95")}),-1.0]])]});
            var sketch = newSketch(context, id + "F43", { "sketchPlane" : qUnion([Q0])});
            skLineSegment(sketch, "E110", {"start": v(-1553.14, 3434.73) * mm, "end": v(1546.86, 3434.73) * mm});
            skLineSegment(sketch, "E111", {"start": v(1546.86, 3434.73) * mm, "end": v(1546.86, 2188.73) * mm});
            skLineSegment(sketch, "E112", {"start": v(1546.86, 2188.73) * mm, "end": v(545.86, 2188.73) * mm});
            skLineSegment(sketch, "E113", {"start": v(545.86, 2188.73) * mm, "end": v(545.86, -1091.27) * mm});
            skLineSegment(sketch, "E114", {"start": v(-1553.14, 3434.73) * mm, "end": v(-1553.14, -1091.27) * mm});
            skLineSegment(sketch, "E115", {"start": v(-1553.14, -1091.27) * mm, "end": v(545.86, -1091.27) * mm});
            skSolve(sketch);
        }
        {
            var Q0;
            Q0=qSketchRegion(id+"F43",true);
            extrude(context, id + "F44", {"entities" : qUnion([Q0]), "operationType" : NewBodyOperationType.ADD, "depth" : 2700 * mm});
        }
        {
            var Q0;
            Q0=makeQuery(id+"F44.opExtrude","SWEPT_FACE",FACE,{"disambiguationData":[OSD([sQuery(id+"F43.wireOp",EDGE,"E114")])]});
            var sketch = newSketch(context, id + "F45", { "sketchPlane" : qUnion([Q0])});
            skLineSegment(sketch, "E116.bottom", {"start": v(-3238.73, 5300) * mm, "end": v(-1213.73, 5300) * mm});
            skLineSegment(sketch, "E116.top", {"start": v(-3238.73, 3900) * mm, "end": v(-1213.73, 3900) * mm});
            skLineSegment(sketch, "E116.left", {"start": v(-3238.73, 5300) * mm, "end": v(-3238.73, 3900) * mm});
            skLineSegment(sketch, "E116.right", {"start": v(-1213.73, 5300) * mm, "end": v(-1213.73, 3900) * mm});
            skSolve(sketch);
        }
        {
            var Q0;
            Q0=qSketchRegion(id+"F45",true);
            extrude(context, id + "F46", {"entities" : qUnion([Q0]), "operationType" : NewBodyOperationType.ADD, "depth" : 533 * mm});
        }
        {
            var Q0;
            Q0=makeQuery(id+"F44.opExtrude","SWEPT_FACE",FACE,{"disambiguationData":[OSD([sQuery(id+"F43.wireOp",EDGE,"E110")])]});
            var sketch = newSketch(context, id + "F47", { "sketchPlane" : qUnion([Q0])});
            skLineSegment(sketch, "E117.bottom", {"start": v(-1009.86, 5300) * mm, "end": v(1015.14, 5300) * mm});
            skLineSegment(sketch, "E117.top", {"start": v(-1009.86, 3900) * mm, "end": v(1015.14, 3900) * mm});
            skLineSegment(sketch, "E117.left", {"start": v(-1009.86, 5300) * mm, "end": v(-1009.86, 3900) * mm});
            skLineSegment(sketch, "E117.right", {"start": v(1015.14, 5300) * mm, "end": v(1015.14, 3900) * mm});
            skSolve(sketch);
        }
        {
            var Q0;
            Q0=qSketchRegion(id+"F47",true);
            extrude(context, id + "F48", {"entities" : qUnion([Q0]), "operationType" : NewBodyOperationType.ADD, "depth" : 532 * mm});
        }
        {
            var Q0;
            Q0=makeQuery(id+"F39.opExtrude","SWEPT_FACE",FACE,{"disambiguationData":[OSD([sQuery(id+"F38.wireOp",EDGE,"E102")])]});
            var sketch = newSketch(context, id + "F49", { "sketchPlane" : qUnion([Q0])});
            skLineSegment(sketch, "E118.bottom", {"start": v(926.73, 5100) * mm, "end": v(1776.73, 5100) * mm});
            skLineSegment(sketch, "E118.top", {"start": v(926.73, 3000) * mm, "end": v(1776.73, 3000) * mm});
            skLineSegment(sketch, "E118.left", {"start": v(926.73, 5100) * mm, "end": v(926.73, 3000) * mm});
            skLineSegment(sketch, "E118.right", {"start": v(1776.73, 5100) * mm, "end": v(1776.73, 3000) * mm});
            skSolve(sketch);
        }
        {
            var Q0;
            Q0=makeQuery(id+"F49.imprint","IMPRINT",FACE,{"disambiguationData":[TD([[makeQuery(id+"F49.imprint","IMPRINT",EDGE,{"derivedFrom":sQuery(id+"F49.wireOp",EDGE,"E118.bottom")}),-1.0]])]});
            extrude(context, id + "F50", {"entities" : qUnion([Q0]), "operationType" : NewBodyOperationType.ADD, "depth" : 255 * mm});
        }
        {
            var Q0;
            Q0=makeQuery(id+"F39.opExtrude","SWEPT_FACE",FACE,{"disambiguationData":[OSD([sQuery(id+"F20.wireOp",EDGE,"E23.bottom"),sQuery(id+"F38.wireOp",EDGE,"E95")])]});
            var sketch = newSketch(context, id + "F51", { "sketchPlane" : qUnion([Q0])});
            skLineSegment(sketch, "E119.bottom", {"start": v(-5105.86, 3000) * mm, "end": v(-4255.86, 3000) * mm});
            skLineSegment(sketch, "E119.top", {"start": v(-5105.86, 5100) * mm, "end": v(-4255.86, 5100) * mm});
            skLineSegment(sketch, "E119.left", {"start": v(-5105.86, 3000) * mm, "end": v(-5105.86, 5100) * mm});
            skLineSegment(sketch, "E119.right", {"start": v(-4255.86, 3000) * mm, "end": v(-4255.86, 5100) * mm});
            skSolve(sketch);
        }
        {
            var Q0;
            Q0=qSketchRegion(id+"F51",true);
            var Q1;
            Q1=makeQuery(id+"F51.imprint","IMPRINT",FACE,{"disambiguationData":[TD([[makeQuery(id+"F51.imprint","IMPRINT",EDGE,{"derivedFrom":sQuery(id+"F51.wireOp",EDGE,"E119.bottom")}),-1.0]])]});
            extrude(context, id + "F52", {"entities" : qUnion([Q0, Q1]), "operationType" : NewBodyOperationType.ADD, "depth" : 160 * mm});
        }
        {
            var Q0;
            Q0=makeQuery(id+"F39.opExtrude","SWEPT_FACE",FACE,{"disambiguationData":[OSD([sQuery(id+"F38.wireOp",EDGE,"E105")])]});
            var sketch = newSketch(context, id + "F53", { "sketchPlane" : qUnion([Q0])});
            skLineSegment(sketch, "E120.bottom", {"start": v(2596.28, 3000) * mm, "end": v(3446.28, 3000) * mm});
            skLineSegment(sketch, "E120.top", {"start": v(2596.28, 5100) * mm, "end": v(3446.28, 5100) * mm});
            skLineSegment(sketch, "E120.left", {"start": v(2596.28, 3000) * mm, "end": v(2596.28, 5100) * mm});
            skLineSegment(sketch, "E120.right", {"start": v(3446.28, 3000) * mm, "end": v(3446.28, 5100) * mm});
            skSolve(sketch);
        }
        {
            var Q0;
            Q0=makeQuery(id+"F53.imprint","IMPRINT",FACE,{"disambiguationData":[TD([[makeQuery(id+"F53.imprint","IMPRINT",EDGE,{"derivedFrom":sQuery(id+"F53.wireOp",EDGE,"E120.bottom")}),1.0]])]});
            extrude(context, id + "F54", {"entities" : qUnion([Q0]), "operationType" : NewBodyOperationType.ADD, "depth" : 250 * mm});
        }
        {
            var Q0;
            Q0=makeQuery(id+"F43.imprint","IMPRINT",FACE,{"disambiguationData":[TD([[makeQuery(id+"F43.imprint","IMPRINT",EDGE,{"derivedFrom":makeQuery(id+"F38.imprint","IMPRINT",EDGE,{"derivedFrom":sQuery(id+"F38.wireOp",EDGE,"E95")})}),-1.0]])]});
            var sketch = newSketch(context, id + "F55", { "sketchPlane" : qUnion([Q0])});
            skLineSegment(sketch, "E121", {"start": v(1765.86, 3404.73) * mm, "end": v(1765.86, 2158.73) * mm});
            skLineSegment(sketch, "E122", {"start": v(1765.86, 2158.73) * mm, "end": v(4191.86, 2158.73) * mm});
            skLineSegment(sketch, "E123", {"start": v(4191.86, 2158.73) * mm, "end": v(4191.86, 747.73) * mm});
            skLineSegment(sketch, "E124", {"start": v(4191.86, 747.73) * mm, "end": v(7471.86, 747.73) * mm});
            skLineSegment(sketch, "E125", {"start": v(7471.86, 747.73) * mm, "end": v(7471.86, 3404.73) * mm});
            skLineSegment(sketch, "E126", {"start": v(7471.86, 3404.73) * mm, "end": v(1765.86, 3404.73) * mm});
            skSolve(sketch);
        }
        {
            var Q0;
            Q0=makeQuery(id+"F55.imprint","IMPRINT",FACE,{"disambiguationData":[TD([[makeQuery(id+"F55.imprint","IMPRINT",EDGE,{"derivedFrom":sQuery(id+"F55.wireOp",EDGE,"E121")}),1.0]])]});
            extrude(context, id + "F56", {"entities" : qUnion([Q0]), "operationType" : NewBodyOperationType.ADD, "depth" : 2700 * mm});
        }
        {
            var Q0;
            Q0=makeQuery(id+"F56.opExtrude","SWEPT_FACE",FACE,{"disambiguationData":[OSD([sQuery(id+"F55.wireOp",EDGE,"E126")])]});
            var sketch = newSketch(context, id + "F57", { "sketchPlane" : qUnion([Q0])});
            skLineSegment(sketch, "E127.bottom", {"start": v(-6883.86, 5300) * mm, "end": v(-4783.86, 5300) * mm});
            skLineSegment(sketch, "E127.top", {"start": v(-6883.86, 3900) * mm, "end": v(-4783.86, 3900) * mm});
            skLineSegment(sketch, "E127.left", {"start": v(-6883.86, 5300) * mm, "end": v(-6883.86, 3900) * mm});
            skLineSegment(sketch, "E127.right", {"start": v(-4783.86, 5300) * mm, "end": v(-4783.86, 3900) * mm});
            skSolve(sketch);
        }
        {
            var Q0;
            Q0=makeQuery(id+"F57.imprint","IMPRINT",FACE,{"disambiguationData":[TD([[makeQuery(id+"F57.imprint","IMPRINT",EDGE,{"derivedFrom":sQuery(id+"F57.wireOp",EDGE,"E127.bottom")}),-1.0]])]});
            extrude(context, id + "F58", {"entities" : qUnion([Q0]), "operationType" : NewBodyOperationType.ADD, "depth" : 532 * mm});
        }
        {
            var Q0;
            Q0=makeQuery(id+"F43.imprint","IMPRINT",FACE,{"disambiguationData":[TD([[makeQuery(id+"F43.imprint","IMPRINT",EDGE,{"derivedFrom":makeQuery(id+"F38.imprint","IMPRINT",EDGE,{"derivedFrom":sQuery(id+"F38.wireOp",EDGE,"E95")})}),-1.0]])]});
            var sketch = newSketch(context, id + "F59", { "sketchPlane" : qUnion([Q0])});
            skLineSegment(sketch, "E128", {"start": v(-1549.14, -1375.27) * mm, "end": v(-1549.14, -3872.27) * mm});
            skLineSegment(sketch, "E129", {"start": v(-1549.14, -3872.27) * mm, "end": v(1546.86, -3872.27) * mm});
            skLineSegment(sketch, "E130", {"start": v(1546.86, -3872.27) * mm, "end": v(1546.86, -3512.03) * mm});
            skLineSegment(sketch, "E131", {"start": v(-1549.14, -1375.27) * mm, "end": v(540.86, -1375.27) * mm});
            skLineSegment(sketch, "E132", {"start": v(540.86, -1375.27) * mm, "end": v(540.86, -2519.58) * mm});
            skLineSegment(sketch, "E133", {"start": v(540.86, -2519.58) * mm, "end": v(1546.86, -3512.03) * mm});
            skSolve(sketch);
        }
        {
            var Q0;
            Q0=qSketchRegion(id+"F59",true);
            extrude(context, id + "F60", {"entities" : qUnion([Q0]), "operationType" : NewBodyOperationType.ADD, "depth" : 2700 * mm});
        }
        {
            var Q0;
            {var subQ0=sQuery(id+"F20.wireOp",EDGE,"E23.bottom");var subQ1=sQuery(id+"F20.wireOp",EDGE,"E23.left");Q0=makeQuery(id+"F56.boolean.opBoolean","MERGE",FACE,{"derivedFrom":[makeQuery(id+"F54.boolean.opBoolean","MERGE",FACE,{"derivedFrom":[makeQuery(id+"F52.boolean.opBoolean","MERGE",FACE,{"derivedFrom":[makeQuery(id+"F50.boolean.opBoolean","MERGE",FACE,{"derivedFrom":[makeQuery(id+"F44.boolean.opBoolean","MERGE",FACE,{"derivedFrom":[makeQuery(id+"F42.boolean.opBoolean","MERGE",FACE,{"derivedFrom":[makeQuery(id+"F40.opBoolean","MERGE",FACE,{"derivedFrom":[makeQuery(id+"F39.opExtrude","CAP_FACE",FACE,{"disambiguationData":[OSD([subQ0,sQuery(id+"F20.wireOp",EDGE,"E23.top"),subQ1,sQuery(id+"F20.wireOp",EDGE,"E23.right")])],"isStart":true}),makeQuery(id+"F39.opExtrude","CAP_FACE",FACE,{"disambiguationData":[OSD([subQ0,subQ1,sQuery(id+"F38.wireOp",EDGE,"E95"),sQuery(id+"F38.wireOp",EDGE,"E96"),sQuery(id+"F38.wireOp",EDGE,"E97"),sQuery(id+"F38.wireOp",EDGE,"E98"),sQuery(id+"F38.wireOp",EDGE,"E99"),sQuery(id+"F38.wireOp",EDGE,"E100"),sQuery(id+"F38.wireOp",EDGE,"E101"),sQuery(id+"F38.wireOp",EDGE,"E102"),sQuery(id+"F38.wireOp",EDGE,"E103"),sQuery(id+"F38.wireOp",EDGE,"E104"),sQuery(id+"F38.wireOp",EDGE,"E105"),sQuery(id+"F38.wireOp",EDGE,"E106"),sQuery(id+"F38.wireOp",EDGE,"E107")])],"isStart":true})]}),makeQuery(id+"F42.opExtrude","SWEPT_FACE",FACE,{"disambiguationData":[OSD([sQuery(id+"F41.wireOp",EDGE,"E109.top")])]})]}),makeQuery(id+"F44.opExtrude","CAP_FACE",FACE,{"disambiguationData":[OSD([sQuery(id+"F43.wireOp",EDGE,"E110"),sQuery(id+"F43.wireOp",EDGE,"E111"),sQuery(id+"F43.wireOp",EDGE,"E112"),sQuery(id+"F43.wireOp",EDGE,"E113"),sQuery(id+"F43.wireOp",EDGE,"E114"),sQuery(id+"F43.wireOp",EDGE,"E115")])],"isStart":true})]}),makeQuery(id+"F50.opExtrude","SWEPT_FACE",FACE,{"disambiguationData":[OSD([sQuery(id+"F49.wireOp",EDGE,"E118.top")])]})]}),makeQuery(id+"F52.opExtrude","SWEPT_FACE",FACE,{"disambiguationData":[OSD([sQuery(id+"F51.wireOp",EDGE,"E119.bottom")])]})]}),makeQuery(id+"F54.opExtrude","SWEPT_FACE",FACE,{"disambiguationData":[OSD([sQuery(id+"F53.wireOp",EDGE,"E120.bottom")])]})]}),makeQuery(id+"F56.opExtrude","CAP_FACE",FACE,{"disambiguationData":[OSD([sQuery(id+"F55.wireOp",EDGE,"E121"),sQuery(id+"F55.wireOp",EDGE,"E122"),sQuery(id+"F55.wireOp",EDGE,"E123"),sQuery(id+"F55.wireOp",EDGE,"E124"),sQuery(id+"F55.wireOp",EDGE,"E125"),sQuery(id+"F55.wireOp",EDGE,"E126")])],"isStart":true})]});}
            var sketch = newSketch(context, id + "F61", { "sketchPlane" : qUnion([Q0])});
            skLineSegment(sketch, "E134", {"start": v(4255.86, 2314.27) * mm, "end": v(4255.86, -563.73) * mm});
            skLineSegment(sketch, "E135", {"start": v(4255.86, -563.73) * mm, "end": v(7408.86, -563.73) * mm});
            skLineSegment(sketch, "E136", {"start": v(7408.86, -563.73) * mm, "end": v(7471.86, -563.73) * mm});
            skLineSegment(sketch, "E137", {"start": v(7471.86, -563.73) * mm, "end": v(7471.86, 5091.27) * mm});
            skLineSegment(sketch, "E138", {"start": v(7471.86, 5091.27) * mm, "end": v(5480.86, 5091.27) * mm});
            skLineSegment(sketch, "E139", {"start": v(5480.86, 5091.27) * mm, "end": v(5480.86, 2314.27) * mm});
            skLineSegment(sketch, "E140", {"start": v(5480.86, 2314.27) * mm, "end": v(4255.86, 2314.27) * mm});
            skSolve(sketch);
        }
        {
            var Q0;
            {var subQ2=sQuery(id+"F61.wireOp",EDGE,"E134");Q0=makeQuery(id+"F61.imprint","IMPRINT",FACE,{"disambiguationData":[TD([[makeQuery(id+"F61.imprint","IMPRINT",EDGE,{"derivedFrom":subQ2}),1.0]])]});}
            extrude(context, id + "F62", {"entities" : qUnion([Q0]), "operationType" : NewBodyOperationType.ADD, "oppositeDirection" : true, "depth" : 2700 * mm});
        }
        {
            var Q0;
            Q0=makeQuery(id+"F56.opExtrude","SWEPT_FACE",FACE,{"disambiguationData":[OSD([sQuery(id+"F55.wireOp",EDGE,"E125")])]});
            var sketch = newSketch(context, id + "F63", { "sketchPlane" : qUnion([Q0])});
            skLineSegment(sketch, "E141.bottom", {"start": v(1183.73, 5300) * mm, "end": v(3208.73, 5300) * mm});
            skLineSegment(sketch, "E141.top", {"start": v(1183.73, 3900) * mm, "end": v(3208.73, 3900) * mm});
            skLineSegment(sketch, "E141.left", {"start": v(1183.73, 5300) * mm, "end": v(1183.73, 3900) * mm});
            skLineSegment(sketch, "E141.right", {"start": v(3208.73, 5300) * mm, "end": v(3208.73, 3900) * mm});
            skSolve(sketch);
        }
        {
            var Q0;
            Q0=makeQuery(id+"F63.imprint","IMPRINT",FACE,{"disambiguationData":[TD([[makeQuery(id+"F63.imprint","IMPRINT",EDGE,{"derivedFrom":sQuery(id+"F63.wireOp",EDGE,"E141.bottom")}),-1.0]])]});
            extrude(context, id + "F64", {"entities" : qUnion([Q0]), "operationType" : NewBodyOperationType.ADD, "depth" : 532 * mm});
        }
        {
            var Q0;
            Q0=makeQuery(id+"F62.opExtrude","SWEPT_FACE",FACE,{"disambiguationData":[OSD([sQuery(id+"F61.wireOp",EDGE,"E137")])]});
            var sketch = newSketch(context, id + "F65", { "sketchPlane" : qUnion([Q0])});
            skLineSegment(sketch, "E142.bottom", {"start": v(-3767.27, 5300) * mm, "end": v(-1742.27, 5300) * mm});
            skLineSegment(sketch, "E142.top", {"start": v(-3767.27, 3900) * mm, "end": v(-1742.27, 3900) * mm});
            skLineSegment(sketch, "E142.left", {"start": v(-3767.27, 5300) * mm, "end": v(-3767.27, 3900) * mm});
            skLineSegment(sketch, "E142.right", {"start": v(-1742.27, 5300) * mm, "end": v(-1742.27, 3900) * mm});
            skSolve(sketch);
        }
        {
            var Q0;
            Q0=makeQuery(id+"F65.imprint","IMPRINT",FACE,{"disambiguationData":[TD([[makeQuery(id+"F65.imprint","IMPRINT",EDGE,{"derivedFrom":sQuery(id+"F65.wireOp",EDGE,"E142.bottom")}),-1.0]])]});
            extrude(context, id + "F66", {"entities" : qUnion([Q0]), "operationType" : NewBodyOperationType.ADD, "depth" : 532 * mm});
        }
        {
            var Q0;
            Q0=makeQuery(id+"F60.opExtrude","SWEPT_FACE",FACE,{"disambiguationData":[OSD([sQuery(id+"F59.wireOp",EDGE,"E129")])]});
            var sketch = newSketch(context, id + "F67", { "sketchPlane" : qUnion([Q0])});
            skLineSegment(sketch, "E143.bottom", {"start": v(-1134.15, 5300) * mm, "end": v(890.85, 5300) * mm});
            skLineSegment(sketch, "E143.top", {"start": v(-1134.15, 3900) * mm, "end": v(890.85, 3900) * mm});
            skLineSegment(sketch, "E143.left", {"start": v(-1134.15, 5300) * mm, "end": v(-1134.15, 3900) * mm});
            skLineSegment(sketch, "E143.right", {"start": v(890.85, 5300) * mm, "end": v(890.85, 3900) * mm});
            skSolve(sketch);
        }
        {
            var Q0;
            Q0=makeQuery(id+"F67.imprint","IMPRINT",FACE,{"disambiguationData":[TD([[makeQuery(id+"F67.imprint","IMPRINT",EDGE,{"derivedFrom":sQuery(id+"F67.wireOp",EDGE,"E143.bottom")}),-1.0]])]});
            extrude(context, id + "F68", {"entities" : qUnion([Q0]), "operationType" : NewBodyOperationType.ADD, "depth" : 532 * mm});
        }
        {
            var Q0;
            Q0=makeQuery(id+"F39.opExtrude","SWEPT_FACE",FACE,{"disambiguationData":[OSD([sQuery(id+"F38.wireOp",EDGE,"E97")])]});
            var sketch = newSketch(context, id + "F69", { "sketchPlane" : qUnion([Q0])});
            skLineSegment(sketch, "E144.bottom", {"start": v(2647.86, 5300) * mm, "end": v(4447.86, 5300) * mm});
            skLineSegment(sketch, "E144.top", {"start": v(2647.86, 3900) * mm, "end": v(4447.86, 3900) * mm});
            skLineSegment(sketch, "E144.left", {"start": v(2647.86, 5300) * mm, "end": v(2647.86, 3900) * mm});
            skLineSegment(sketch, "E144.right", {"start": v(4447.86, 5300) * mm, "end": v(4447.86, 3900) * mm});
            skSolve(sketch);
        }
        {
            var Q0;
            Q0=makeQuery(id+"F69.imprint","IMPRINT",FACE,{"disambiguationData":[TD([[makeQuery(id+"F69.imprint","IMPRINT",EDGE,{"derivedFrom":sQuery(id+"F69.wireOp",EDGE,"E144.bottom")}),-1.0]])]});
            extrude(context, id + "F70", {"entities" : qUnion([Q0]), "operationType" : NewBodyOperationType.ADD, "depth" : 532 * mm});
        }
        {
            var Q0;
            Q0=makeQuery(id+"F3.opExtrude","CAP_EDGE",EDGE,{"disambiguationData":[OSD([sQuery(id+"F2.wireOp",EDGE,"E1.top")])],"isStart":false});
            chamfer(context, id + "F71", {"entities" : qUnion([Q0]), "width" : 10 * mm, "tangentPropagation" : true});
        }
        {
            var Q0;
            Q0=makeQuery(id+"F60.opExtrude","SWEPT_FACE",FACE,{"disambiguationData":[OSD([sQuery(id+"F59.wireOp",EDGE,"E128")])]});
            var sketch = newSketch(context, id + "F72", { "sketchPlane" : qUnion([Q0])});
            skCircle(sketch, "E145", {"center": v(1775.27, 5450) * mm, "radius": 150 * mm});
            skSolve(sketch);
        }
        {
            var Q0;
            Q0=makeQuery(id+"F19.opExtrude","CAP_EDGE",EDGE,{"disambiguationData":[OSD([sQuery(id+"F18.wireOp",EDGE,"E22.top")])],"isStart":true});
            chamfer(context, id + "F73", {"entities" : qUnion([Q0]), "width" : 10 * mm, "tangentPropagation" : true});
        }
        {
            var Q0;
            Q0=makeQuery(id+"F1.opExtrude","SWEPT_FACE",FACE,{"disambiguationData":[OSD([sQuery(id+"F0.wireOp",EDGE,"E0.left")])]});
            var sketch = newSketch(context, id + "F74", { "sketchPlane" : qUnion([Q0])});
            skLineSegment(sketch, "E146.left", {"start": v(-3238.73, 860) * mm, "end": v(-3238.73, 60) * mm});
            skLineSegment(sketch, "E147.bottom", {"start": v(-3238.73, 860) * mm, "end": v(-1213.73, 860) * mm});
            skLineSegment(sketch, "E147.top", {"start": v(-3238.73, 60) * mm, "end": v(-1213.73, 60) * mm});
            skLineSegment(sketch, "E147.right", {"start": v(-1213.73, 860) * mm, "end": v(-1213.73, 60) * mm});
            skSolve(sketch);
        }
        {
            var Q0;
            Q0=makeQuery(id+"F66.opExtrude","CAP_EDGE",EDGE,{"disambiguationData":[OSD([sQuery(id+"F65.wireOp",EDGE,"E142.top")])],"isStart":false});
            chamfer(context, id + "F75", {"entities" : qUnion([Q0]), "width" : 10 * mm, "tangentPropagation" : true});
        }
        {
            var Q0;
            Q0=makeQuery(id+"F64.opExtrude","CAP_EDGE",EDGE,{"disambiguationData":[OSD([sQuery(id+"F63.wireOp",EDGE,"E141.top")])],"isStart":false});
            chamfer(context, id + "F76", {"entities" : qUnion([Q0]), "width" : 10 * mm, "tangentPropagation" : true});
        }
        {
            var Q0;
            Q0=makeQuery(id+"F68.opExtrude","CAP_EDGE",EDGE,{"disambiguationData":[OSD([sQuery(id+"F67.wireOp",EDGE,"E143.top")])],"isStart":false});
            var Q1;
            Q1=makeQuery(id+"F70.opExtrude","CAP_EDGE",EDGE,{"disambiguationData":[OSD([sQuery(id+"F69.wireOp",EDGE,"E144.top")])],"isStart":false});
            var Q2;
            Q2=makeQuery(id+"F15.opExtrude","CAP_EDGE",EDGE,{"disambiguationData":[OSD([sQuery(id+"F14.wireOp",EDGE,"E13.top")])],"isStart":false});
            var Q3;
            Q3=makeQuery(id+"F46.opExtrude","CAP_EDGE",EDGE,{"disambiguationData":[OSD([sQuery(id+"F45.wireOp",EDGE,"E116.top")])],"isStart":false});
            var Q4;
            Q4=makeQuery(id+"F5.opExtrude","CAP_EDGE",EDGE,{"disambiguationData":[OSD([sQuery(id+"F4.wireOp",EDGE,"E2.top")])],"isStart":false});
            var Q5;
            Q5=makeQuery(id+"F58.opExtrude","CAP_EDGE",EDGE,{"disambiguationData":[OSD([sQuery(id+"F57.wireOp",EDGE,"E127.top")])],"isStart":false});
            var Q6;
            Q6=makeQuery(id+"F48.opExtrude","CAP_EDGE",EDGE,{"disambiguationData":[OSD([sQuery(id+"F47.wireOp",EDGE,"E117.top")])],"isStart":false});
            var Q7;
            Q7=makeQuery(id+"F29.opExtrude","CAP_EDGE",EDGE,{"disambiguationData":[OSD([sQuery(id+"F28.wireOp",EDGE,"E91.top")])],"isStart":false});
            var Q8;
            Q8=makeQuery(id+"F37.opExtrude","CAP_EDGE",EDGE,{"disambiguationData":[OSD([sQuery(id+"F36.wireOp",EDGE,"E94.bottom")])],"isStart":false});
            var Q9;
            Q9=makeQuery(id+"F68.opExtrude","CAP_EDGE",EDGE,{"disambiguationData":[OSD([sQuery(id+"F67.wireOp",EDGE,"E143.left")])],"isStart":false});
            var Q10;
            Q10=makeQuery(id+"F68.opExtrude","CAP_EDGE",EDGE,{"disambiguationData":[OSD([sQuery(id+"F67.wireOp",EDGE,"E143.right")])],"isStart":false});
            var Q11;
            Q11=makeQuery(id+"F68.opExtrude","CAP_EDGE",EDGE,{"disambiguationData":[OSD([sQuery(id+"F67.wireOp",EDGE,"E143.bottom")])],"isStart":false});
            var Q12;
            Q12=makeQuery(id+"F70.opExtrude","CAP_EDGE",EDGE,{"disambiguationData":[OSD([sQuery(id+"F69.wireOp",EDGE,"E144.left")])],"isStart":false});
            var Q13;
            Q13=makeQuery(id+"F70.opExtrude","CAP_EDGE",EDGE,{"disambiguationData":[OSD([sQuery(id+"F69.wireOp",EDGE,"E144.bottom")])],"isStart":false});
            var Q14;
            Q14=makeQuery(id+"F70.opExtrude","CAP_EDGE",EDGE,{"disambiguationData":[OSD([sQuery(id+"F69.wireOp",EDGE,"E144.right")])],"isStart":false});
            var Q15;
            Q15=makeQuery(id+"F15.opExtrude","CAP_EDGE",EDGE,{"disambiguationData":[OSD([sQuery(id+"F14.wireOp",EDGE,"E13.left")])],"isStart":false});
            var Q16;
            Q16=makeQuery(id+"F15.opExtrude","CAP_EDGE",EDGE,{"disambiguationData":[OSD([sQuery(id+"F14.wireOp",EDGE,"E13.bottom")])],"isStart":false});
            var Q17;
            Q17=makeQuery(id+"F15.opExtrude","CAP_EDGE",EDGE,{"disambiguationData":[OSD([sQuery(id+"F14.wireOp",EDGE,"E13.right")])],"isStart":false});
            var Q18;
            Q18=makeQuery(id+"F5.opExtrude","CAP_EDGE",EDGE,{"disambiguationData":[OSD([sQuery(id+"F4.wireOp",EDGE,"E2.bottom")])],"isStart":false});
            var Q19;
            Q19=makeQuery(id+"F5.opExtrude","CAP_EDGE",EDGE,{"disambiguationData":[OSD([sQuery(id+"F4.wireOp",EDGE,"E2.right")])],"isStart":false});
            var Q20;
            Q20=makeQuery(id+"F5.opExtrude","CAP_EDGE",EDGE,{"disambiguationData":[OSD([sQuery(id+"F4.wireOp",EDGE,"E2.left")])],"isStart":false});
            var Q21;
            Q21=makeQuery(id+"F46.opExtrude","CAP_EDGE",EDGE,{"disambiguationData":[OSD([sQuery(id+"F45.wireOp",EDGE,"E116.left")])],"isStart":false});
            var Q22;
            Q22=makeQuery(id+"F46.opExtrude","CAP_EDGE",EDGE,{"disambiguationData":[OSD([sQuery(id+"F45.wireOp",EDGE,"E116.bottom")])],"isStart":false});
            var Q23;
            Q23=makeQuery(id+"F46.opExtrude","CAP_EDGE",EDGE,{"disambiguationData":[OSD([sQuery(id+"F45.wireOp",EDGE,"E116.right")])],"isStart":false});
            var Q24;
            Q24=makeQuery(id+"F3.opExtrude","CAP_EDGE",EDGE,{"disambiguationData":[OSD([sQuery(id+"F2.wireOp",EDGE,"E1.bottom")])],"isStart":false});
            var Q25;
            Q25=makeQuery(id+"F3.opExtrude","CAP_EDGE",EDGE,{"disambiguationData":[OSD([sQuery(id+"F2.wireOp",EDGE,"E1.left")])],"isStart":false});
            var Q26;
            Q26=makeQuery(id+"F3.opExtrude","CAP_EDGE",EDGE,{"disambiguationData":[OSD([sQuery(id+"F2.wireOp",EDGE,"E1.right")])],"isStart":false});
            var Q27;
            {var subQ0=sQuery(id+"F2.wireOp",EDGE,"E1.top");Q27=makeQuery(id+"F71.opChamfer","BLEND_EDGE",EDGE,{"blendedFrom":[makeQuery(id+"F3.opExtrude","CAP_EDGE",EDGE,{"disambiguationData":[OSD([subQ0])],"isStart":false}),makeQuery(id+"F3.opExtrude","CAP_FACE",FACE,{"disambiguationData":[OSD([sQuery(id+"F2.wireOp",EDGE,"E1.bottom"),subQ0,sQuery(id+"F2.wireOp",EDGE,"E1.left"),sQuery(id+"F2.wireOp",EDGE,"E1.right")])],"isStart":false})],"blendedInto":[makeQuery(id+"F3.opExtrude","CAP_FACE",FACE,{"disambiguationData":[OSD([sQuery(id+"F2.wireOp",EDGE,"E1.bottom"),subQ0,sQuery(id+"F2.wireOp",EDGE,"E1.left"),sQuery(id+"F2.wireOp",EDGE,"E1.right")])],"isStart":false})]});}
            var Q28;
            Q28=makeQuery(id+"F48.opExtrude","CAP_EDGE",EDGE,{"disambiguationData":[OSD([sQuery(id+"F47.wireOp",EDGE,"E117.left")])],"isStart":false});
            var Q29;
            Q29=makeQuery(id+"F48.opExtrude","CAP_EDGE",EDGE,{"disambiguationData":[OSD([sQuery(id+"F47.wireOp",EDGE,"E117.right")])],"isStart":false});
            var Q30;
            Q30=makeQuery(id+"F48.opExtrude","CAP_EDGE",EDGE,{"disambiguationData":[OSD([sQuery(id+"F47.wireOp",EDGE,"E117.bottom")])],"isStart":false});
            var Q31;
            Q31=makeQuery(id+"F58.opExtrude","CAP_EDGE",EDGE,{"disambiguationData":[OSD([sQuery(id+"F57.wireOp",EDGE,"E127.bottom")])],"isStart":false});
            var Q32;
            Q32=makeQuery(id+"F58.opExtrude","CAP_EDGE",EDGE,{"disambiguationData":[OSD([sQuery(id+"F57.wireOp",EDGE,"E127.right")])],"isStart":false});
            var Q33;
            Q33=makeQuery(id+"F58.opExtrude","CAP_EDGE",EDGE,{"disambiguationData":[OSD([sQuery(id+"F57.wireOp",EDGE,"E127.left")])],"isStart":false});
            var Q34;
            Q34=makeQuery(id+"F29.opExtrude","CAP_EDGE",EDGE,{"disambiguationData":[OSD([sQuery(id+"F28.wireOp",EDGE,"E91.right")])],"isStart":false});
            var Q35;
            Q35=makeQuery(id+"F29.opExtrude","CAP_EDGE",EDGE,{"disambiguationData":[OSD([sQuery(id+"F28.wireOp",EDGE,"E91.bottom")])],"isStart":false});
            var Q36;
            Q36=makeQuery(id+"F29.opExtrude","CAP_EDGE",EDGE,{"disambiguationData":[OSD([sQuery(id+"F28.wireOp",EDGE,"E91.left")])],"isStart":false});
            var Q37;
            Q37=makeQuery(id+"F64.opExtrude","CAP_EDGE",EDGE,{"disambiguationData":[OSD([sQuery(id+"F63.wireOp",EDGE,"E141.bottom")])],"isStart":false});
            var Q38;
            Q38=makeQuery(id+"F66.opExtrude","CAP_EDGE",EDGE,{"disambiguationData":[OSD([sQuery(id+"F65.wireOp",EDGE,"E142.bottom")])],"isStart":false});
            var Q39;
            Q39=makeQuery(id+"F66.opExtrude","CAP_EDGE",EDGE,{"disambiguationData":[OSD([sQuery(id+"F65.wireOp",EDGE,"E142.right")])],"isStart":false});
            var Q40;
            {var subQ0=sQuery(id+"F65.wireOp",EDGE,"E142.top");Q40=makeQuery(id+"F75.opChamfer","BLEND_EDGE",EDGE,{"blendedFrom":[makeQuery(id+"F66.opExtrude","CAP_EDGE",EDGE,{"disambiguationData":[OSD([subQ0])],"isStart":false}),makeQuery(id+"F66.opExtrude","CAP_FACE",FACE,{"disambiguationData":[OSD([sQuery(id+"F65.wireOp",EDGE,"E142.bottom"),subQ0,sQuery(id+"F65.wireOp",EDGE,"E142.left"),sQuery(id+"F65.wireOp",EDGE,"E142.right")])],"isStart":false})],"blendedInto":[makeQuery(id+"F66.opExtrude","CAP_FACE",FACE,{"disambiguationData":[OSD([sQuery(id+"F65.wireOp",EDGE,"E142.bottom"),subQ0,sQuery(id+"F65.wireOp",EDGE,"E142.left"),sQuery(id+"F65.wireOp",EDGE,"E142.right")])],"isStart":false})]});}
            var Q41;
            Q41=makeQuery(id+"F66.opExtrude","CAP_EDGE",EDGE,{"disambiguationData":[OSD([sQuery(id+"F65.wireOp",EDGE,"E142.left")])],"isStart":false});
            var Q42;
            Q42=makeQuery(id+"F19.opExtrude","SWEPT_EDGE",EDGE,{"disambiguationData":[OSD([sQuery(id+"F18.wireOp",EDGE,"E22.top"),sQuery(id+"F18.wireOp",EDGE,"E22.left")])]});
            var Q43;
            Q43=makeQuery(id+"F19.opExtrude","CAP_EDGE",EDGE,{"disambiguationData":[OSD([sQuery(id+"F18.wireOp",EDGE,"E22.top")])],"isStart":false});
            var Q44;
            Q44=makeQuery(id+"F19.opExtrude","SWEPT_EDGE",EDGE,{"disambiguationData":[OSD([sQuery(id+"F18.wireOp",EDGE,"E22.top"),sQuery(id+"F18.wireOp",EDGE,"E22.right")])]});
            chamfer(context, id + "F77", {"entities" : qUnion([Q0, Q1, Q2, Q3, Q4, Q5, Q6, Q7, Q8, Q9, Q10, Q11, Q12, Q13, Q14, Q15, Q16, Q17, Q18, Q19, Q20, Q21, Q22, Q23, Q24, Q25, Q26, Q27, Q28, Q29, Q30, Q31, Q32, Q33, Q34, Q35, Q36, Q37, Q38, Q39, Q40, Q41, Q42, Q43, Q44]), "width" : 10 * mm, "tangentPropagation" : true});
        }
        {
            var Q0;
            Q0=makeQuery(id+"F1.opExtrude","SWEPT_FACE",FACE,{"disambiguationData":[OSD([sQuery(id+"F0.wireOp",EDGE,"E0.bottom")])]});
            var sketch = newSketch(context, id + "F78", { "sketchPlane" : qUnion([Q0])});
            skLineSegment(sketch, "E148", {"start": v(-1013.86, 900) * mm, "end": v(1011.14, 900) * mm});
            skLineSegment(sketch, "E149", {"start": v(1011.14, 900) * mm, "end": v(1011.14, 870) * mm});
            skLineSegment(sketch, "E150", {"start": v(1011.14, 870) * mm, "end": v(-1013.86, 870) * mm});
            skLineSegment(sketch, "E151", {"start": v(-1013.86, 870) * mm, "end": v(-1013.86, 900) * mm});
            skSolve(sketch);
        }
        {
            var Q0;
            Q0=makeQuery(id+"F78.imprint","IMPRINT",FACE,{"disambiguationData":[TD([[makeQuery(id+"F78.imprint","IMPRINT",EDGE,{"derivedFrom":sQuery(id+"F78.wireOp",EDGE,"E148")}),-1.0]])]});
            extrude(context, id + "F79", {"entities" : qUnion([Q0]), "operationType" : NewBodyOperationType.REMOVE, "oppositeDirection" : true, "depth" : 200 * mm});
        }
        {
            var Q0;
            Q0=makeQuery(id+"F27.opExtrude","SWEPT_FACE",FACE,{"disambiguationData":[OSD([sQuery(id+"F26.wireOp",EDGE,"E75"),sQuery(id+"F26.wireOp",EDGE,"E76"),sQuery(id+"F26.wireOp",EDGE,"E86")])]});
            var sketch = newSketch(context, id + "F80", { "sketchPlane" : qUnion([Q0])});
            skLineSegment(sketch, "E152", {"start": v(-6883.86, 900) * mm, "end": v(-4883.86, 900) * mm});
            skLineSegment(sketch, "E153", {"start": v(-4883.86, 900) * mm, "end": v(-4883.86, 870) * mm});
            skLineSegment(sketch, "E154", {"start": v(-4883.86, 870) * mm, "end": v(-6883.86, 870) * mm});
            skLineSegment(sketch, "E155", {"start": v(-6883.86, 870) * mm, "end": v(-6883.86, 900) * mm});
            skSolve(sketch);
        }
        {
            var Q0;
            Q0=qSketchRegion(id+"F80",true);
            extrude(context, id + "F81", {"entities" : qUnion([Q0]), "operationType" : NewBodyOperationType.REMOVE, "oppositeDirection" : true, "depth" : 200 * mm});
        }
        {
            var Q0;
            Q0=makeQuery(id+"F56.opExtrude","SWEPT_FACE",FACE,{"disambiguationData":[OSD([sQuery(id+"F55.wireOp",EDGE,"E126")])]});
            var sketch = newSketch(context, id + "F82", { "sketchPlane" : qUnion([Q0])});
            skLineSegment(sketch, "E156", {"start": v(-6883.86, 3900) * mm, "end": v(-4783.86, 3900) * mm});
            skLineSegment(sketch, "E157", {"start": v(-4783.86, 3900) * mm, "end": v(-4783.86, 3870) * mm});
            skLineSegment(sketch, "E158", {"start": v(-4783.86, 3870) * mm, "end": v(-6883.86, 3870) * mm});
            skLineSegment(sketch, "E159", {"start": v(-6883.86, 3870) * mm, "end": v(-6883.86, 3900) * mm});
            skSolve(sketch);
        }
        {
            var Q0;
            Q0=qSketchRegion(id+"F82",true);
            extrude(context, id + "F83", {"entities" : qUnion([Q0]), "operationType" : NewBodyOperationType.REMOVE, "oppositeDirection" : true, "depth" : 185 * mm});
        }
        {
            var Q0;
            Q0=makeQuery(id+"F44.opExtrude","SWEPT_FACE",FACE,{"disambiguationData":[OSD([sQuery(id+"F43.wireOp",EDGE,"E110")])]});
            var sketch = newSketch(context, id + "F84", { "sketchPlane" : qUnion([Q0])});
            skLineSegment(sketch, "E160.bottom", {"start": v(-1009.86, 3900) * mm, "end": v(1015.14, 3900) * mm});
            skLineSegment(sketch, "E160.top", {"start": v(-1009.86, 3870) * mm, "end": v(1015.14, 3870) * mm});
            skLineSegment(sketch, "E160.left", {"start": v(-1009.86, 3900) * mm, "end": v(-1009.86, 3870) * mm});
            skLineSegment(sketch, "E160.right", {"start": v(1015.14, 3900) * mm, "end": v(1015.14, 3870) * mm});
            skLineSegment(sketch, "E161.bottom", {"start": v(1015.14, 3870) * mm, "end": v(1015.14, 3870) * mm});
            skLineSegment(sketch, "E161.top", {"start": v(1015.14, 3900) * mm, "end": v(1015.14, 3900) * mm});
            skLineSegment(sketch, "E161.left", {"start": v(1015.14, 3870) * mm, "end": v(1015.14, 3900) * mm});
            skLineSegment(sketch, "E161.right", {"start": v(1015.14, 3870) * mm, "end": v(1015.14, 3900) * mm});
            skSolve(sketch);
        }
        {
            var Q0;
            Q0=makeQuery(id+"F84.imprint","IMPRINT",FACE,{"disambiguationData":[TD([[makeQuery(id+"F84.imprint","IMPRINT",EDGE,{"derivedFrom":sQuery(id+"F84.wireOp",EDGE,"E160.bottom")}),-1.0]])]});
            extrude(context, id + "F85", {"entities" : qUnion([Q0]), "operationType" : NewBodyOperationType.REMOVE, "oppositeDirection" : true, "depth" : 180 * mm});
        }
        {
            var Q0;
            Q0=makeQuery(id+"F44.opExtrude","SWEPT_FACE",FACE,{"disambiguationData":[OSD([sQuery(id+"F43.wireOp",EDGE,"E114")])]});
            var sketch = newSketch(context, id + "F86", { "sketchPlane" : qUnion([Q0])});
            skLineSegment(sketch, "E162.bottom", {"start": v(-3238.73, 3900) * mm, "end": v(-1213.73, 3900) * mm});
            skLineSegment(sketch, "E162.top", {"start": v(-3238.73, 3870) * mm, "end": v(-1213.73, 3870) * mm});
            skLineSegment(sketch, "E162.left", {"start": v(-3238.73, 3900) * mm, "end": v(-3238.73, 3870) * mm});
            skLineSegment(sketch, "E162.right", {"start": v(-1213.73, 3900) * mm, "end": v(-1213.73, 3870) * mm});
            skSolve(sketch);
        }
        {
            var Q0;
            Q0=qSketchRegion(id+"F86",true);
            extrude(context, id + "F87", {"entities" : qUnion([Q0]), "operationType" : NewBodyOperationType.REMOVE, "oppositeDirection" : true, "depth" : 200 * mm});
        }
        {
            var Q0;
            Q0=makeQuery(id+"F60.opExtrude","SWEPT_FACE",FACE,{"disambiguationData":[OSD([sQuery(id+"F59.wireOp",EDGE,"E129")])]});
            var sketch = newSketch(context, id + "F88", { "sketchPlane" : qUnion([Q0])});
            skLineSegment(sketch, "E163.bottom", {"start": v(-1134.15, 3900) * mm, "end": v(890.85, 3900) * mm});
            skLineSegment(sketch, "E163.top", {"start": v(-1134.15, 3870) * mm, "end": v(890.85, 3870) * mm});
            skLineSegment(sketch, "E163.left", {"start": v(-1134.15, 3900) * mm, "end": v(-1134.15, 3870) * mm});
            skLineSegment(sketch, "E163.right", {"start": v(890.85, 3900) * mm, "end": v(890.85, 3870) * mm});
            skSolve(sketch);
        }
        {
            var Q0;
            Q0=makeQuery(id+"F88.imprint","IMPRINT",FACE,{"disambiguationData":[TD([[makeQuery(id+"F88.imprint","IMPRINT",EDGE,{"derivedFrom":sQuery(id+"F88.wireOp",EDGE,"E163.bottom")}),-1.0]])]});
            extrude(context, id + "F89", {"entities" : qUnion([Q0]), "operationType" : NewBodyOperationType.REMOVE, "oppositeDirection" : true, "depth" : 180 * mm});
        }
        {
            var Q0;
            Q0=makeQuery(id+"F17.boolean.opBoolean","MERGE",FACE,{"derivedFrom":[makeQuery(id+"F13.boolean.opBoolean","MERGE",FACE,{"derivedFrom":[makeQuery(id+"F11.opExtrude","SWEPT_FACE",FACE,{"disambiguationData":[OSD([sQuery(id+"F10.wireOp",EDGE,"E10.top")])]}),makeQuery(id+"F13.opExtrude","SWEPT_FACE",FACE,{"disambiguationData":[OSD([sQuery(id+"F12.wireOp",EDGE,"E12.bottom")])]})]}),makeQuery(id+"F17.opExtrude","SWEPT_FACE",FACE,{"disambiguationData":[OSD([sQuery(id+"F16.wireOp",EDGE,"E14")])]})]});
            var sketch = newSketch(context, id + "F90", { "sketchPlane" : qUnion([Q0])});
            skLineSegment(sketch, "E164.bottom", {"start": v(-1134.15, 896.53) * mm, "end": v(890.85, 896.53) * mm});
            skLineSegment(sketch, "E164.top", {"start": v(-1134.15, 866.53) * mm, "end": v(890.85, 866.53) * mm});
            skLineSegment(sketch, "E164.left", {"start": v(-1134.15, 896.53) * mm, "end": v(-1134.15, 866.53) * mm});
            skLineSegment(sketch, "E164.right", {"start": v(890.85, 896.53) * mm, "end": v(890.85, 866.53) * mm});
            skSolve(sketch);
        }
        {
            var Q0;
            Q0=makeQuery(id+"F90.imprint","IMPRINT",FACE,{"disambiguationData":[TD([[makeQuery(id+"F90.imprint","IMPRINT",EDGE,{"derivedFrom":sQuery(id+"F90.wireOp",EDGE,"E164.bottom")}),-1.0]])]});
            extrude(context, id + "F91", {"entities" : qUnion([Q0]), "operationType" : NewBodyOperationType.REMOVE, "oppositeDirection" : true, "depth" : 180 * mm});
        }
        {
            var Q0;
            Q0=makeQuery(id+"F39.opExtrude","SWEPT_FACE",FACE,{"disambiguationData":[OSD([sQuery(id+"F38.wireOp",EDGE,"E97")])]});
            var sketch = newSketch(context, id + "F92", { "sketchPlane" : qUnion([Q0])});
            skLineSegment(sketch, "E165.bottom", {"start": v(2647.86, 3900) * mm, "end": v(4447.86, 3900) * mm});
            skLineSegment(sketch, "E165.top", {"start": v(2647.86, 3870) * mm, "end": v(4447.86, 3870) * mm});
            skLineSegment(sketch, "E165.left", {"start": v(2647.86, 3900) * mm, "end": v(2647.86, 3870) * mm});
            skLineSegment(sketch, "E165.right", {"start": v(4447.86, 3900) * mm, "end": v(4447.86, 3870) * mm});
            skSolve(sketch);
        }
        {
            var Q0;
            Q0=makeQuery(id+"F62.opExtrude","SWEPT_FACE",FACE,{"disambiguationData":[OSD([sQuery(id+"F61.wireOp",EDGE,"E137")])]});
            var sketch = newSketch(context, id + "F93", { "sketchPlane" : qUnion([Q0])});
            skLineSegment(sketch, "E166.bottom", {"start": v(-3767.27, 3900) * mm, "end": v(-1742.27, 3900) * mm});
            skLineSegment(sketch, "E166.top", {"start": v(-3767.27, 3870) * mm, "end": v(-1742.27, 3870) * mm});
            skLineSegment(sketch, "E166.left", {"start": v(-3767.27, 3900) * mm, "end": v(-3767.27, 3870) * mm});
            skLineSegment(sketch, "E166.right", {"start": v(-1742.27, 3900) * mm, "end": v(-1742.27, 3870) * mm});
            skSolve(sketch);
        }
        {
            var Q0;
            Q0=makeQuery(id+"F93.imprint","IMPRINT",FACE,{"disambiguationData":[TD([[makeQuery(id+"F93.imprint","IMPRINT",EDGE,{"derivedFrom":sQuery(id+"F93.wireOp",EDGE,"E166.bottom")}),-1.0]])]});
            extrude(context, id + "F94", {"entities" : qUnion([Q0]), "operationType" : NewBodyOperationType.REMOVE, "oppositeDirection" : true, "depth" : 180 * mm});
        }
        {
            var Q0;
            Q0=makeQuery(id+"F56.opExtrude","SWEPT_FACE",FACE,{"disambiguationData":[OSD([sQuery(id+"F55.wireOp",EDGE,"E125")])]});
            var sketch = newSketch(context, id + "F95", { "sketchPlane" : qUnion([Q0])});
            skLineSegment(sketch, "E167.bottom", {"start": v(1183.73, 3900) * mm, "end": v(3208.73, 3900) * mm});
            skLineSegment(sketch, "E167.top", {"start": v(1183.73, 3870) * mm, "end": v(3208.73, 3870) * mm});
            skLineSegment(sketch, "E167.left", {"start": v(1183.73, 3900) * mm, "end": v(1183.73, 3870) * mm});
            skLineSegment(sketch, "E167.right", {"start": v(3208.73, 3900) * mm, "end": v(3208.73, 3870) * mm});
            skSolve(sketch);
        }
        {
            var Q0;
            Q0=makeQuery(id+"F95.imprint","IMPRINT",FACE,{"disambiguationData":[TD([[makeQuery(id+"F95.imprint","IMPRINT",EDGE,{"derivedFrom":sQuery(id+"F95.wireOp",EDGE,"E167.bottom")}),-1.0]])]});
            extrude(context, id + "F96", {"entities" : qUnion([Q0]), "operationType" : NewBodyOperationType.REMOVE, "oppositeDirection" : true, "depth" : 180 * mm});
        }
        {
            var Q0;
            Q0=makeQuery(id+"F27.opExtrude","SWEPT_FACE",FACE,{"disambiguationData":[OSD([sQuery(id+"F26.wireOp",EDGE,"E89")])]});
            var sketch = newSketch(context, id + "F97", { "sketchPlane" : qUnion([Q0])});
            skCircle(sketch, "E168", {"center": v(1837.73, 2430) * mm, "radius": 150 * mm});
            skSolve(sketch);
        }
        {
            var Q0;
            Q0=makeQuery(id+"F74.imprint","IMPRINT",FACE,{"disambiguationData":[TD([[makeQuery(id+"F74.imprint","IMPRINT",EDGE,{"derivedFrom":sQuery(id+"F74.wireOp",EDGE,"E147.bottom")}),-1.0]])]});
            extrude(context, id + "F98", {"entities" : qUnion([Q0]), "operationType" : NewBodyOperationType.REMOVE, "oppositeDirection" : true, "depth" : 200 * mm});
        }
        {
            var Q0;
            {var subQ0=sQuery(id+"F0.wireOp",EDGE,"E0.left");var subQ1=sQuery(id+"F0.wireOp",EDGE,"E0.bottom");Q0=makeQuery(id+"F98.boolean.opBoolean","SPLIT",FACE,{"disambiguationData":[TD([makeQuery(id+"F1.opExtrude","SWEPT_FACE",FACE,{"disambiguationData":[OSD([subQ1])]})])],"derivedFrom":makeQuery(id+"F1.opExtrude","SWEPT_FACE",FACE,{"disambiguationData":[OSD([subQ0])]})});}
            var sketch = newSketch(context, id + "F99", { "sketchPlane" : qUnion([Q0])});
            skLineSegment(sketch, "E169.bottom", {"start": v(-3238.73, 900) * mm, "end": v(-1213.73, 900) * mm});
            skLineSegment(sketch, "E169.top", {"start": v(-3238.73, 870) * mm, "end": v(-1213.73, 870) * mm});
            skLineSegment(sketch, "E169.left", {"start": v(-3238.73, 900) * mm, "end": v(-3238.73, 870) * mm});
            skLineSegment(sketch, "E169.right", {"start": v(-1213.73, 900) * mm, "end": v(-1213.73, 870) * mm});
            skSolve(sketch);
        }
        {
            var Q0;
            Q0=makeQuery(id+"F99.imprint","IMPRINT",FACE,{"disambiguationData":[TD([[makeQuery(id+"F99.imprint","IMPRINT",EDGE,{"derivedFrom":sQuery(id+"F99.wireOp",EDGE,"E169.bottom")}),-1.0]])]});
            extrude(context, id + "F100", {"entities" : qUnion([Q0]), "operationType" : NewBodyOperationType.REMOVE, "oppositeDirection" : true, "depth" : 200 * mm});
        }
        {
            var Q0;
            Q0=qSketchRegion(id+"F92",true);
            extrude(context, id + "F101", {"entities" : qUnion([Q0]), "operationType" : NewBodyOperationType.REMOVE, "oppositeDirection" : true, "depth" : 180 * mm});
        }
        {
            var Q0;
            Q0=makeQuery(id+"F17.boolean.opBoolean","MERGE",FACE,{"derivedFrom":[makeQuery(id+"F13.boolean.opBoolean","MERGE",FACE,{"derivedFrom":[makeQuery(id+"F11.opExtrude","SWEPT_FACE",FACE,{"disambiguationData":[OSD([sQuery(id+"F10.wireOp",EDGE,"E10.top")])]}),makeQuery(id+"F13.opExtrude","SWEPT_FACE",FACE,{"disambiguationData":[OSD([sQuery(id+"F12.wireOp",EDGE,"E12.bottom")])]})]}),makeQuery(id+"F17.opExtrude","SWEPT_FACE",FACE,{"disambiguationData":[OSD([sQuery(id+"F16.wireOp",EDGE,"E14")])]})]});
            var sketch = newSketch(context, id + "F102", { "sketchPlane" : qUnion([Q0])});
            skLineSegment(sketch, "E170.left", {"start": v(-1134.15, 841.53) * mm, "end": v(-1134.15, 41.53) * mm});
            skLineSegment(sketch, "E171.bottom", {"start": v(-1134.15, 841.53) * mm, "end": v(890.85, 841.53) * mm});
            skLineSegment(sketch, "E171.top", {"start": v(-1134.15, 41.53) * mm, "end": v(890.85, 41.53) * mm});
            skLineSegment(sketch, "E171.right", {"start": v(890.85, 841.53) * mm, "end": v(890.85, 41.53) * mm});
            skSolve(sketch);
        }
        {
            var Q0;
            Q0 = qSketchRegion(id + "F102", true);
            extrude(context, id + "F103", {"entities" : qUnion([Q0]), "operationType" : NewBodyOperationType.REMOVE, "oppositeDirection" : true, "depth" : 200 * mm});
        }
        {
            var Q0;
            Q0=makeQuery(id+"F60.opExtrude","SWEPT_FACE",FACE,{"disambiguationData":[OSD([sQuery(id+"F59.wireOp",EDGE,"E129")])]});
            var sketch = newSketch(context, id + "F104", { "sketchPlane" : qUnion([Q0])});
            skLineSegment(sketch, "E172.left", {"start": v(-1134.15, 3850) * mm, "end": v(-1134.15, 3050) * mm});
            skLineSegment(sketch, "E173.bottom", {"start": v(-1134.15, 3850) * mm, "end": v(890.85, 3850) * mm});
            skLineSegment(sketch, "E173.top", {"start": v(-1134.15, 3050) * mm, "end": v(890.85, 3050) * mm});
            skLineSegment(sketch, "E173.right", {"start": v(890.85, 3850) * mm, "end": v(890.85, 3050) * mm});
            skSolve(sketch);
        }
        {
            var Q0;
            Q0=makeQuery(id+"F104.imprint","IMPRINT",FACE,{"disambiguationData":[TD([[makeQuery(id+"F104.imprint","IMPRINT",EDGE,{"derivedFrom":sQuery(id+"F104.wireOp",EDGE,"E173.bottom")}),-1.0]])]});
            extrude(context, id + "F105", {"entities" : qUnion([Q0]), "operationType" : NewBodyOperationType.REMOVE, "oppositeDirection" : true, "depth" : 200 * mm});
        }
        {
            var Q0;
            Q0=makeQuery(id+"F27.opExtrude","SWEPT_FACE",FACE,{"disambiguationData":[OSD([sQuery(id+"F26.wireOp",EDGE,"E75"),sQuery(id+"F26.wireOp",EDGE,"E76"),sQuery(id+"F26.wireOp",EDGE,"E86")])]});
            var sketch = newSketch(context, id + "F106", { "sketchPlane" : qUnion([Q0])});
            skLineSegment(sketch, "E174.left", {"start": v(-6833.86, 3808.27) * mm, "end": v(-6833.86, 3081.73) * mm});
            skLineSegment(sketch, "E175.bottom", {"start": v(-6833.86, 3808.27) * mm, "end": v(-4833.86, 3808.27) * mm});
            skLineSegment(sketch, "E175.top", {"start": v(-6833.86, 3081.73) * mm, "end": v(-4833.86, 3081.73) * mm});
            skLineSegment(sketch, "E175.right", {"start": v(-4833.86, 3808.27) * mm, "end": v(-4833.86, 3081.73) * mm});
            skSolve(sketch);
        }
        {
            var Q0;
            Q0=makeQuery(id+"F106.imprint","IMPRINT",FACE,{"disambiguationData":[TD([[makeQuery(id+"F106.imprint","IMPRINT",EDGE,{"derivedFrom":sQuery(id+"F106.wireOp",EDGE,"E175.bottom")}),-1.0]])]});
            extrude(context, id + "F107", {"entities" : qUnion([Q0]), "operationType" : NewBodyOperationType.REMOVE, "oppositeDirection" : true, "depth" : 200 * mm});
        }
        {
            var Q0;
            Q0=makeQuery(id+"F44.opExtrude","SWEPT_FACE",FACE,{"disambiguationData":[OSD([sQuery(id+"F43.wireOp",EDGE,"E110")])]});
            var sketch = newSketch(context, id + "F108", { "sketchPlane" : qUnion([Q0])});
            skLineSegment(sketch, "E176.left", {"start": v(-1009.86, 3845) * mm, "end": v(-1009.86, 3045) * mm});
            skLineSegment(sketch, "E177.bottom", {"start": v(-1009.86, 3845) * mm, "end": v(1015.14, 3845) * mm});
            skLineSegment(sketch, "E177.top", {"start": v(-1009.86, 3045) * mm, "end": v(1015.14, 3045) * mm});
            skLineSegment(sketch, "E177.right", {"start": v(1015.14, 3845) * mm, "end": v(1015.14, 3045) * mm});
            skSolve(sketch);
        }
        {
            var Q0;
            Q0=makeQuery(id+"F108.imprint","IMPRINT",FACE,{"disambiguationData":[TD([[makeQuery(id+"F108.imprint","IMPRINT",EDGE,{"derivedFrom":sQuery(id+"F108.wireOp",EDGE,"E177.bottom")}),-1.0]])]});
            extrude(context, id + "F109", {"entities" : qUnion([Q0]), "operationType" : NewBodyOperationType.REMOVE, "oppositeDirection" : true, "depth" : 200 * mm});
        }
        {
            var Q0;
            Q0=makeQuery(id+"F44.opExtrude","SWEPT_FACE",FACE,{"disambiguationData":[OSD([sQuery(id+"F43.wireOp",EDGE,"E114")])]});
            var sketch = newSketch(context, id + "F110", { "sketchPlane" : qUnion([Q0])});
            skLineSegment(sketch, "E178.left", {"start": v(-3238.73, 3845) * mm, "end": v(-3238.73, 3045) * mm});
            skLineSegment(sketch, "E179.bottom", {"start": v(-3238.73, 3845) * mm, "end": v(-1213.73, 3845) * mm});
            skLineSegment(sketch, "E179.top", {"start": v(-3238.73, 3045) * mm, "end": v(-1213.73, 3045) * mm});
            skLineSegment(sketch, "E179.right", {"start": v(-1213.73, 3845) * mm, "end": v(-1213.73, 3045) * mm});
            skSolve(sketch);
        }
        {
            var Q0;
            Q0=makeQuery(id+"F110.imprint","IMPRINT",FACE,{"disambiguationData":[TD([[makeQuery(id+"F110.imprint","IMPRINT",EDGE,{"derivedFrom":sQuery(id+"F110.wireOp",EDGE,"E179.bottom")}),-1.0]])]});
            extrude(context, id + "F111", {"entities" : qUnion([Q0]), "operationType" : NewBodyOperationType.REMOVE, "oppositeDirection" : true, "depth" : 200 * mm});
        }
        {
            var Q0;
            Q0=makeQuery(id+"F27.opExtrude","SWEPT_FACE",FACE,{"disambiguationData":[OSD([sQuery(id+"F26.wireOp",EDGE,"E75"),sQuery(id+"F26.wireOp",EDGE,"E76"),sQuery(id+"F26.wireOp",EDGE,"E86")])]});
            var sketch = newSketch(context, id + "F112", { "sketchPlane" : qUnion([Q0])});
            skLineSegment(sketch, "E180.bottom", {"start": v(-6883.86, 845) * mm, "end": v(-4883.86, 845) * mm});
            skLineSegment(sketch, "E180.top", {"start": v(-6883.86, 45) * mm, "end": v(-4883.86, 45) * mm});
            skLineSegment(sketch, "E180.right", {"start": v(-4883.86, 845) * mm, "end": v(-4883.86, 45) * mm});
            skLineSegment(sketch, "E181", {"start": v(-6883.86, 845) * mm, "end": v(-6883.86, 45) * mm});
            skSolve(sketch);
        }
        {
            var Q0;
            Q0=makeQuery(id+"F112.imprint","IMPRINT",FACE,{"disambiguationData":[TD([[makeQuery(id+"F112.imprint","IMPRINT",EDGE,{"derivedFrom":sQuery(id+"F112.wireOp",EDGE,"E180.bottom")}),-1.0]])]});
            extrude(context, id + "F113", {"entities" : qUnion([Q0]), "operationType" : NewBodyOperationType.REMOVE, "oppositeDirection" : true, "depth" : 200 * mm});
        }
        {
            var Q0;
            Q0=makeQuery(id+"F56.opExtrude","SWEPT_FACE",FACE,{"disambiguationData":[OSD([sQuery(id+"F55.wireOp",EDGE,"E125")])]});
            var sketch = newSketch(context, id + "F114", { "sketchPlane" : qUnion([Q0])});
            skLineSegment(sketch, "E182.left", {"start": v(1183.73, 3845) * mm, "end": v(1183.73, 3045) * mm});
            skLineSegment(sketch, "E183.bottom", {"start": v(1183.73, 3845) * mm, "end": v(3208.73, 3845) * mm});
            skLineSegment(sketch, "E183.top", {"start": v(1183.73, 3045) * mm, "end": v(3208.73, 3045) * mm});
            skLineSegment(sketch, "E183.right", {"start": v(3208.73, 3845) * mm, "end": v(3208.73, 3045) * mm});
            skSolve(sketch);
        }
        {
            var Q0;
            Q0=makeQuery(id+"F114.imprint","IMPRINT",FACE,{"disambiguationData":[TD([[makeQuery(id+"F114.imprint","IMPRINT",EDGE,{"derivedFrom":sQuery(id+"F114.wireOp",EDGE,"E183.bottom")}),-1.0]])]});
            extrude(context, id + "F115", {"entities" : qUnion([Q0]), "operationType" : NewBodyOperationType.REMOVE, "oppositeDirection" : true, "depth" : 200 * mm});
        }
        {
            var Q0;
            Q0=makeQuery(id+"F62.opExtrude","SWEPT_FACE",FACE,{"disambiguationData":[OSD([sQuery(id+"F61.wireOp",EDGE,"E137")])]});
            var sketch = newSketch(context, id + "F116", { "sketchPlane" : qUnion([Q0])});
            skLineSegment(sketch, "E184.left", {"start": v(-3767.27, 3845) * mm, "end": v(-3767.27, 3045) * mm});
            skLineSegment(sketch, "E185.bottom", {"start": v(-3767.27, 3845) * mm, "end": v(-1742.27, 3845) * mm});
            skLineSegment(sketch, "E185.top", {"start": v(-3767.27, 3045) * mm, "end": v(-1742.27, 3045) * mm});
            skLineSegment(sketch, "E185.right", {"start": v(-1742.27, 3845) * mm, "end": v(-1742.27, 3045) * mm});
            skSolve(sketch);
        }
        {
            var Q0;
            Q0=makeQuery(id+"F116.imprint","IMPRINT",FACE,{"disambiguationData":[TD([[makeQuery(id+"F116.imprint","IMPRINT",EDGE,{"derivedFrom":sQuery(id+"F116.wireOp",EDGE,"E185.bottom")}),-1.0]])]});
            extrude(context, id + "F117", {"entities" : qUnion([Q0]), "operationType" : NewBodyOperationType.REMOVE, "oppositeDirection" : true, "depth" : 200 * mm});
        }
        {
            var Q0;
            Q0=sQuery(id+"F97.wireOp",VERTEX,"E168.center");
            var Q1;
            Q1=qCreatedBy(makeId("Top.planeOp"),FACE);
            cPlane(context, id + "F118", {"entities" : qUnion([Q0, Q1]), "cplaneType" : CPlaneType.PLANE_POINT, "offset" : 25 * mm, "width" : 150 * mm, "height" : 150 * mm});
        }
        {
            var Q0;
            Q0=qCreatedBy(id+"F118.planeOp",FACE);
            var sketch = newSketch(context, id + "F119", { "sketchPlane" : qUnion([Q0])});
            skLineSegment(sketch, "E186.0", {"start": v(7471.86, 1987.73) * mm, "end": v(7471.86, 1687.73) * mm});
            skLineSegment(sketch, "E187", {"start": v(7471.86, 1837.73) * mm, "end": v(7521.86, 1837.73) * mm});
            skLineSegment(sketch, "E188", {"start": v(7721.86, 1637.73) * mm, "end": v(7721.86, 1587.73) * mm});
            skPoint(sketch, "E189.visualSharp", {"position": v(7721.86, 1837.73) * mm});
            skArc(sketch, "E189.filletArc", {"start": v(7721.86, 1637.73) * mm, "mid": v(7663.28, 1779.15) * mm, "end": v(7521.86, 1837.73) * mm});
            skSolve(sketch);
        }
        {
            var Q0;
            Q0=sQuery(id+"F72.wireOp",VERTEX,"E145.center");
            var Q1;
            Q1=qCreatedBy(makeId("Front.planeOp"),FACE);
            cPlane(context, id + "F120", {"entities" : qUnion([Q0, Q1]), "cplaneType" : CPlaneType.PLANE_POINT, "offset" : 25 * mm, "width" : 150 * mm, "height" : 150 * mm});
        }
        {
            var Q0;
            Q0=qCreatedBy(id+"F120.planeOp",FACE);
            var sketch = newSketch(context, id + "F121", { "sketchPlane" : qUnion([Q0])});
            skLineSegment(sketch, "E190.0.0", {"start": v(-1549.14, 5300) * mm, "end": v(-1549.14, 5600) * mm});
            skLineSegment(sketch, "E191", {"start": v(-1549.14, 5450) * mm, "end": v(-1699.14, 5450) * mm});
            skLineSegment(sketch, "E192", {"start": v(-1899.14, 5650) * mm, "end": v(-1899.14, 8240) * mm});
            skPoint(sketch, "E193.visualSharp", {"position": v(-1899.14, 5450) * mm});
            skArc(sketch, "E193.filletArc", {"start": v(-1899.14, 5650) * mm, "mid": v(-1840.56, 5508.58) * mm, "end": v(-1699.14, 5450) * mm});
            skSolve(sketch);
        }
        {
            var Q0;
            Q0=makeQuery(id+"F72.imprint","IMPRINT",FACE,{"disambiguationData":[TD([[makeQuery(id+"F72.imprint","IMPRINT",EDGE,{"derivedFrom":sQuery(id+"F72.wireOp",EDGE,"E145")}),1.0]])]});
            var Q1;
            Q1=sQuery(id+"F121.wireOp",EDGE,"E191");
            var Q2;
            Q2=sQuery(id+"F121.wireOp",EDGE,"E193.filletArc");
            var Q3;
            Q3=sQuery(id+"F121.wireOp",EDGE,"E192");
            sweep(context, id + "F122", {"operationType" : NewBodyOperationType.ADD, "profiles" : qUnion([Q0]), "path" : qUnion([Q1, Q2, Q3])});
        }
        {
            var Q0;
            Q0=qCreatedBy(makeId("Right.planeOp"),FACE);
            var Q1;
            Q1=sQuery(id+"F119.wireOp",VERTEX,"E188.end");
            cPlane(context, id + "F123", {"entities" : qUnion([Q0, Q1]), "cplaneType" : CPlaneType.PLANE_POINT, "offset" : 25 * mm, "width" : 150 * mm, "height" : 150 * mm});
        }
        {
            var Q0;
            Q0=qCreatedBy(id+"F123.planeOp",FACE);
            var sketch = newSketch(context, id + "F124", { "sketchPlane" : qUnion([Q0])});
            skLineSegment(sketch, "E194", {"start": v(1637.73, 2430) * mm, "end": v(887.73, 2430) * mm});
            skLineSegment(sketch, "E195", {"start": v(687.73, 2630) * mm, "end": v(687.73, 8230) * mm});
            skPoint(sketch, "E196.visualSharp", {"position": v(687.73, 2430) * mm});
            skArc(sketch, "E196.filletArc", {"start": v(687.73, 2630) * mm, "mid": v(746.3, 2488.58) * mm, "end": v(887.73, 2430) * mm});
            skPoint(sketch, "E197.0.end.orphan", {"position": v(1837.73, 2430) * mm});
            skPoint(sketch, "E197.0.start.orphan", {"position": v(1637.73, 2430) * mm});
            skSolve(sketch);
        }
        {
            var Q0;
            Q0=makeQuery(id+"F97.imprint","IMPRINT",FACE,{"disambiguationData":[TD([[makeQuery(id+"F97.imprint","IMPRINT",EDGE,{"derivedFrom":sQuery(id+"F97.wireOp",EDGE,"E168")}),1.0]])]});
            var Q1;
            Q1=sQuery(id+"F119.wireOp",EDGE,"E187");
            var Q2;
            Q2=sQuery(id+"F119.wireOp",EDGE,"E189.filletArc");
            var Q3;
            Q3=sQuery(id+"F124.wireOp",EDGE,"E194");
            var Q4;
            Q4=sQuery(id+"F124.wireOp",EDGE,"E196.filletArc");
            var Q5;
            Q5=sQuery(id+"F124.wireOp",EDGE,"E195");
            sweep(context, id + "F125", {"operationType" : NewBodyOperationType.ADD, "profiles" : qUnion([Q0]), "path" : qUnion([Q1, Q2, Q3, Q4, Q5])});
        }
    });
